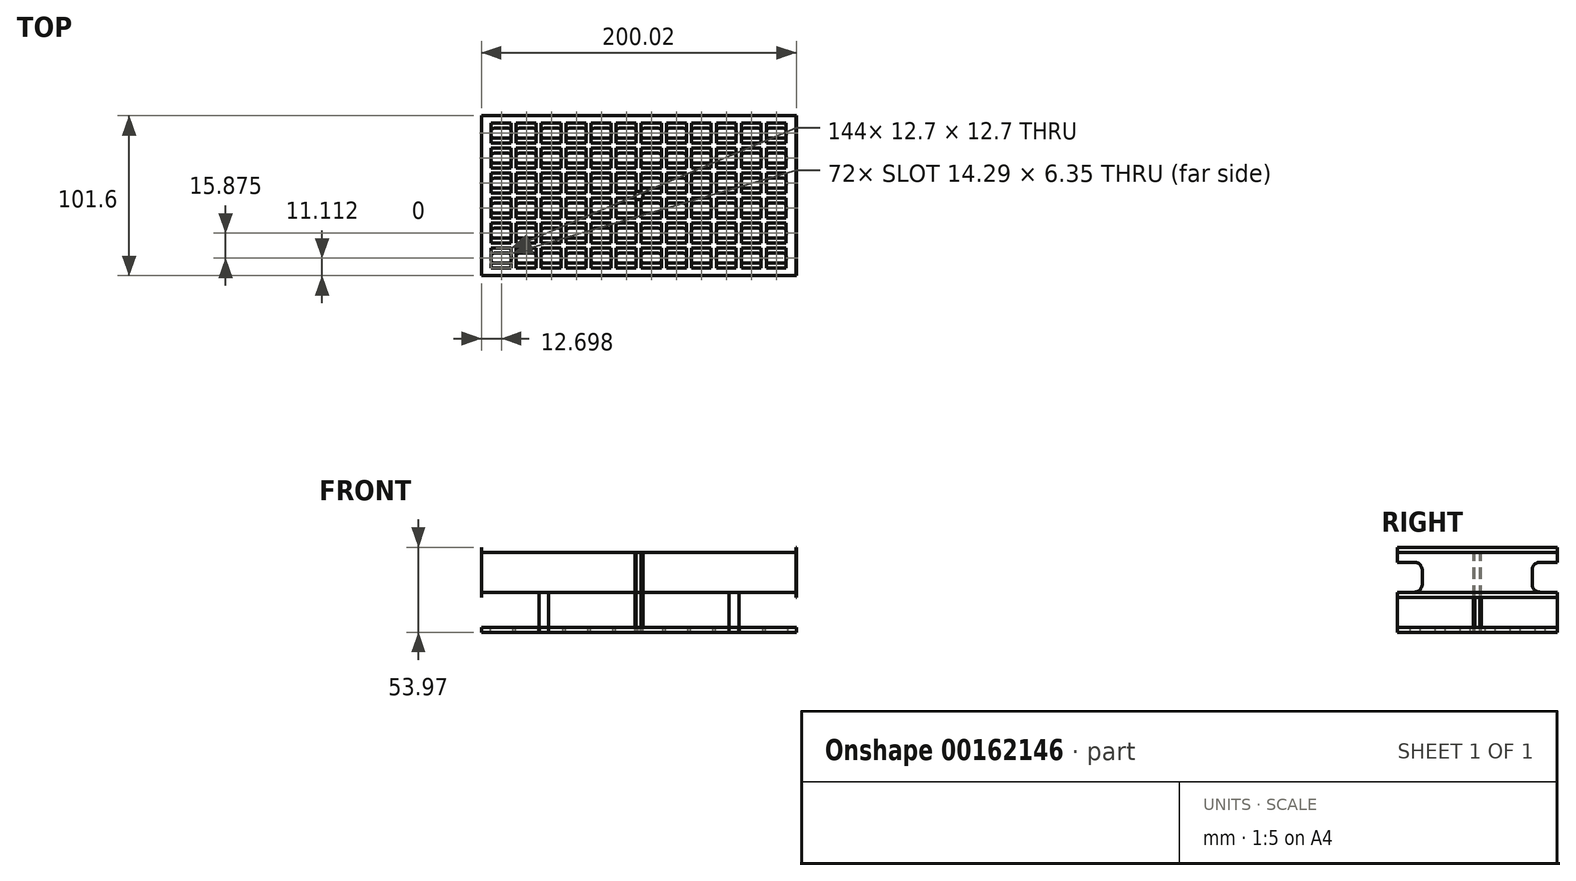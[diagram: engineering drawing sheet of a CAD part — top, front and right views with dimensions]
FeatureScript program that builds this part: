
annotation { "Feature Type Name" : "Feature", "Feature Type Description" : "" }
export const myFeature = defineFeature(function(context is Context, id is Id, definition is map)
    precondition{}
    {
        {
            var Q0;
            Q0=qCreatedBy(makeId("Top.planeOp"),FACE);
            var sketch = newSketch(context, id + "F0", { "sketchPlane" : qUnion([Q0])});
            skLineSegment(sketch, "E0.bottom", {"start": v(100.01, -50.8) * mm, "end": v(-100.01, -50.8) * mm});
            skLineSegment(sketch, "E0.top", {"start": v(100.01, 50.8) * mm, "end": v(-100.01, 50.8) * mm});
            skLineSegment(sketch, "E0.left", {"start": v(100.01, -50.8) * mm, "end": v(100.01, 50.8) * mm});
            skLineSegment(sketch, "E0.right", {"start": v(-100.01, -50.8) * mm, "end": v(-100.01, 50.8) * mm});
            skLineSegment(sketch, "E1", {"start": v(0, 0) * mm, "end": v(-14.29, 0) * mm});
            skLineSegment(sketch, "E2", {"start": v(-14.29, 0) * mm, "end": v(-14.29, -1.59) * mm});
            skLineSegment(sketch, "E3.bottom", {"start": v(-14.29, -1.59) * mm, "end": v(-1.59, -1.59) * mm});
            skLineSegment(sketch, "E3.top", {"start": v(-14.29, -14.29) * mm, "end": v(-1.59, -14.29) * mm});
            skLineSegment(sketch, "E3.left", {"start": v(-14.29, -1.59) * mm, "end": v(-14.29, -14.29) * mm});
            skLineSegment(sketch, "E3.right", {"start": v(-1.59, -1.59) * mm, "end": v(-1.59, -14.29) * mm});
            skLineSegment(sketch, "E4.0.1.0", {"start": v(-14.29, -17.46) * mm, "end": v(-1.59, -17.46) * mm});
            skLineSegment(sketch, "E4.0.1.1", {"start": v(-14.29, -17.46) * mm, "end": v(-14.29, -30.16) * mm});
            skLineSegment(sketch, "E4.0.1.2", {"start": v(-1.59, -17.46) * mm, "end": v(-1.59, -30.16) * mm});
            skLineSegment(sketch, "E4.0.1.3", {"start": v(-14.29, -30.16) * mm, "end": v(-1.59, -30.16) * mm});
            skLineSegment(sketch, "E4.0.2.0", {"start": v(-14.29, -33.34) * mm, "end": v(-1.59, -33.34) * mm});
            skLineSegment(sketch, "E4.0.2.1", {"start": v(-14.29, -33.34) * mm, "end": v(-14.29, -46.04) * mm});
            skLineSegment(sketch, "E4.0.2.2", {"start": v(-1.59, -33.34) * mm, "end": v(-1.59, -46.04) * mm});
            skLineSegment(sketch, "E4.0.2.3", {"start": v(-14.29, -46.04) * mm, "end": v(-1.59, -46.04) * mm});
            skLineSegment(sketch, "E4.1.0.0", {"start": v(-30.16, -1.59) * mm, "end": v(-17.46, -1.59) * mm});
            skLineSegment(sketch, "E4.1.0.1", {"start": v(-30.16, -1.59) * mm, "end": v(-30.16, -14.29) * mm});
            skLineSegment(sketch, "E4.1.0.2", {"start": v(-17.46, -1.59) * mm, "end": v(-17.46, -14.29) * mm});
            skLineSegment(sketch, "E4.1.0.3", {"start": v(-30.16, -14.29) * mm, "end": v(-17.46, -14.29) * mm});
            skLineSegment(sketch, "E4.1.1.0", {"start": v(-30.16, -17.46) * mm, "end": v(-17.46, -17.46) * mm});
            skLineSegment(sketch, "E4.1.1.1", {"start": v(-30.16, -17.46) * mm, "end": v(-30.16, -30.16) * mm});
            skLineSegment(sketch, "E4.1.1.2", {"start": v(-17.46, -17.46) * mm, "end": v(-17.46, -30.16) * mm});
            skLineSegment(sketch, "E4.1.1.3", {"start": v(-30.16, -30.16) * mm, "end": v(-17.46, -30.16) * mm});
            skLineSegment(sketch, "E4.1.2.0", {"start": v(-30.16, -33.34) * mm, "end": v(-17.46, -33.34) * mm});
            skLineSegment(sketch, "E4.1.2.1", {"start": v(-30.16, -33.34) * mm, "end": v(-30.16, -46.04) * mm});
            skLineSegment(sketch, "E4.1.2.2", {"start": v(-17.46, -33.34) * mm, "end": v(-17.46, -46.04) * mm});
            skLineSegment(sketch, "E4.1.2.3", {"start": v(-30.16, -46.04) * mm, "end": v(-17.46, -46.04) * mm});
            skLineSegment(sketch, "E4.2.0.0", {"start": v(-46.04, -1.59) * mm, "end": v(-33.34, -1.59) * mm});
            skLineSegment(sketch, "E4.2.0.1", {"start": v(-46.04, -1.59) * mm, "end": v(-46.04, -14.29) * mm});
            skLineSegment(sketch, "E4.2.0.2", {"start": v(-33.34, -1.59) * mm, "end": v(-33.34, -14.29) * mm});
            skLineSegment(sketch, "E4.2.0.3", {"start": v(-46.04, -14.29) * mm, "end": v(-33.34, -14.29) * mm});
            skLineSegment(sketch, "E4.2.1.0", {"start": v(-46.04, -17.46) * mm, "end": v(-33.34, -17.46) * mm});
            skLineSegment(sketch, "E4.2.1.1", {"start": v(-46.04, -17.46) * mm, "end": v(-46.04, -30.16) * mm});
            skLineSegment(sketch, "E4.2.1.2", {"start": v(-33.34, -17.46) * mm, "end": v(-33.34, -30.16) * mm});
            skLineSegment(sketch, "E4.2.1.3", {"start": v(-46.04, -30.16) * mm, "end": v(-33.34, -30.16) * mm});
            skLineSegment(sketch, "E4.2.2.0", {"start": v(-46.04, -33.34) * mm, "end": v(-33.34, -33.34) * mm});
            skLineSegment(sketch, "E4.2.2.1", {"start": v(-46.04, -33.34) * mm, "end": v(-46.04, -46.04) * mm});
            skLineSegment(sketch, "E4.2.2.2", {"start": v(-33.34, -33.34) * mm, "end": v(-33.34, -46.04) * mm});
            skLineSegment(sketch, "E4.2.2.3", {"start": v(-46.04, -46.04) * mm, "end": v(-33.34, -46.04) * mm});
            skLineSegment(sketch, "E4.3.0.0", {"start": v(-61.91, -1.59) * mm, "end": v(-49.21, -1.59) * mm});
            skLineSegment(sketch, "E4.3.0.1", {"start": v(-61.91, -1.59) * mm, "end": v(-61.91, -14.29) * mm});
            skLineSegment(sketch, "E4.3.0.2", {"start": v(-49.21, -1.59) * mm, "end": v(-49.21, -14.29) * mm});
            skLineSegment(sketch, "E4.3.0.3", {"start": v(-61.91, -14.29) * mm, "end": v(-49.21, -14.29) * mm});
            skLineSegment(sketch, "E4.3.1.0", {"start": v(-61.91, -17.46) * mm, "end": v(-49.21, -17.46) * mm});
            skLineSegment(sketch, "E4.3.1.1", {"start": v(-61.91, -17.46) * mm, "end": v(-61.91, -30.16) * mm});
            skLineSegment(sketch, "E4.3.1.2", {"start": v(-49.21, -17.46) * mm, "end": v(-49.21, -30.16) * mm});
            skLineSegment(sketch, "E4.3.1.3", {"start": v(-61.91, -30.16) * mm, "end": v(-49.21, -30.16) * mm});
            skLineSegment(sketch, "E4.3.2.0", {"start": v(-61.91, -33.34) * mm, "end": v(-49.21, -33.34) * mm});
            skLineSegment(sketch, "E4.3.2.1", {"start": v(-61.91, -33.34) * mm, "end": v(-61.91, -46.04) * mm});
            skLineSegment(sketch, "E4.3.2.2", {"start": v(-49.21, -33.34) * mm, "end": v(-49.21, -46.04) * mm});
            skLineSegment(sketch, "E4.3.2.3", {"start": v(-61.91, -46.04) * mm, "end": v(-49.21, -46.04) * mm});
            skLineSegment(sketch, "E4.4.0.0", {"start": v(-77.79, -1.59) * mm, "end": v(-65.09, -1.59) * mm});
            skLineSegment(sketch, "E4.4.0.1", {"start": v(-77.79, -1.59) * mm, "end": v(-77.79, -14.29) * mm});
            skLineSegment(sketch, "E4.4.0.2", {"start": v(-65.09, -1.59) * mm, "end": v(-65.09, -14.29) * mm});
            skLineSegment(sketch, "E4.4.0.3", {"start": v(-77.79, -14.29) * mm, "end": v(-65.09, -14.29) * mm});
            skLineSegment(sketch, "E4.4.1.0", {"start": v(-77.79, -17.46) * mm, "end": v(-65.09, -17.46) * mm});
            skLineSegment(sketch, "E4.4.1.1", {"start": v(-77.79, -17.46) * mm, "end": v(-77.79, -30.16) * mm});
            skLineSegment(sketch, "E4.4.1.2", {"start": v(-65.09, -17.46) * mm, "end": v(-65.09, -30.16) * mm});
            skLineSegment(sketch, "E4.4.1.3", {"start": v(-77.79, -30.16) * mm, "end": v(-65.09, -30.16) * mm});
            skLineSegment(sketch, "E4.4.2.0", {"start": v(-77.79, -33.34) * mm, "end": v(-65.09, -33.34) * mm});
            skLineSegment(sketch, "E4.4.2.1", {"start": v(-77.79, -33.34) * mm, "end": v(-77.79, -46.04) * mm});
            skLineSegment(sketch, "E4.4.2.2", {"start": v(-65.09, -33.34) * mm, "end": v(-65.09, -46.04) * mm});
            skLineSegment(sketch, "E4.4.2.3", {"start": v(-77.79, -46.04) * mm, "end": v(-65.09, -46.04) * mm});
            skLineSegment(sketch, "E4.5.0.0", {"start": v(-93.66, -1.59) * mm, "end": v(-80.96, -1.59) * mm});
            skLineSegment(sketch, "E4.5.0.1", {"start": v(-93.66, -1.59) * mm, "end": v(-93.66, -14.29) * mm});
            skLineSegment(sketch, "E4.5.0.2", {"start": v(-80.96, -1.59) * mm, "end": v(-80.96, -14.29) * mm});
            skLineSegment(sketch, "E4.5.0.3", {"start": v(-93.66, -14.29) * mm, "end": v(-80.96, -14.29) * mm});
            skLineSegment(sketch, "E4.5.1.0", {"start": v(-93.66, -17.46) * mm, "end": v(-80.96, -17.46) * mm});
            skLineSegment(sketch, "E4.5.1.1", {"start": v(-93.66, -17.46) * mm, "end": v(-93.66, -30.16) * mm});
            skLineSegment(sketch, "E4.5.1.2", {"start": v(-80.96, -17.46) * mm, "end": v(-80.96, -30.16) * mm});
            skLineSegment(sketch, "E4.5.1.3", {"start": v(-93.66, -30.16) * mm, "end": v(-80.96, -30.16) * mm});
            skLineSegment(sketch, "E4.5.2.0", {"start": v(-93.66, -33.34) * mm, "end": v(-80.96, -33.34) * mm});
            skLineSegment(sketch, "E4.5.2.1", {"start": v(-93.66, -33.34) * mm, "end": v(-93.66, -46.04) * mm});
            skLineSegment(sketch, "E4.5.2.2", {"start": v(-80.96, -33.34) * mm, "end": v(-80.96, -46.04) * mm});
            skLineSegment(sketch, "E4.5.2.3", {"start": v(-93.66, -46.04) * mm, "end": v(-80.96, -46.04) * mm});
            skLineSegment(sketch, "E4.direction1", {"start": v(-14.29, -1.59) * mm, "end": v(-30.16, -1.59) * mm, "construction": true});
            skLineSegment(sketch, "E4.direction2", {"start": v(-14.29, -1.59) * mm, "end": v(-14.29, -17.46) * mm, "construction": true});
            skLineSegment(sketch, "E5.MirrorCS", {"start": v(-14.29, 0) * mm, "end": v(-14.29, 1.59) * mm});
            skLineSegment(sketch, "E6.MirrorCS", {"start": v(-30.16, 1.59) * mm, "end": v(-17.46, 1.59) * mm});
            skLineSegment(sketch, "E7.MirrorCS", {"start": v(-14.29, 1.59) * mm, "end": v(-14.29, 14.29) * mm});
            skLineSegment(sketch, "E8.MirrorCS", {"start": v(-93.66, 1.59) * mm, "end": v(-80.96, 1.59) * mm});
            skLineSegment(sketch, "E9.MirrorCS", {"start": v(-46.04, 17.46) * mm, "end": v(-46.04, 30.16) * mm});
            skLineSegment(sketch, "E10.MirrorCS", {"start": v(-93.66, 30.16) * mm, "end": v(-80.96, 30.16) * mm});
            skLineSegment(sketch, "E11.MirrorCS", {"start": v(-30.16, 30.16) * mm, "end": v(-17.46, 30.16) * mm});
            skLineSegment(sketch, "E12.MirrorCS", {"start": v(-46.04, 14.29) * mm, "end": v(-33.34, 14.29) * mm});
            skLineSegment(sketch, "E13.MirrorCS", {"start": v(-61.91, 33.34) * mm, "end": v(-61.91, 46.04) * mm});
            skLineSegment(sketch, "E14.MirrorCS", {"start": v(-61.91, 30.16) * mm, "end": v(-49.21, 30.16) * mm});
            skLineSegment(sketch, "E15.MirrorCS", {"start": v(-93.66, 1.59) * mm, "end": v(-93.66, 14.29) * mm});
            skLineSegment(sketch, "E16.MirrorCS", {"start": v(-30.16, 33.34) * mm, "end": v(-17.46, 33.34) * mm});
            skLineSegment(sketch, "E17.MirrorCS", {"start": v(-80.96, 17.46) * mm, "end": v(-80.96, 30.16) * mm});
            skLineSegment(sketch, "E18.MirrorCS", {"start": v(-17.46, 17.46) * mm, "end": v(-17.46, 30.16) * mm});
            skLineSegment(sketch, "E19.MirrorCS", {"start": v(-61.91, 33.34) * mm, "end": v(-49.21, 33.34) * mm});
            skLineSegment(sketch, "E20.MirrorCS", {"start": v(-46.04, 17.46) * mm, "end": v(-33.34, 17.46) * mm});
            skLineSegment(sketch, "E21.MirrorCS", {"start": v(-1.59, 33.34) * mm, "end": v(-1.59, 46.04) * mm});
            skLineSegment(sketch, "E22.MirrorCS", {"start": v(-46.04, 33.34) * mm, "end": v(-46.04, 46.04) * mm});
            skLineSegment(sketch, "E23.MirrorCS", {"start": v(-1.59, 17.46) * mm, "end": v(-1.59, 30.16) * mm});
            skLineSegment(sketch, "E24.MirrorCS", {"start": v(-14.29, 17.46) * mm, "end": v(-1.59, 17.46) * mm});
            skLineSegment(sketch, "E25.MirrorCS", {"start": v(-14.29, 14.29) * mm, "end": v(-1.59, 14.29) * mm});
            skLineSegment(sketch, "E26.MirrorCS", {"start": v(-14.29, 1.59) * mm, "end": v(-1.59, 1.59) * mm});
            skLineSegment(sketch, "E27.MirrorCS", {"start": v(-14.29, 30.16) * mm, "end": v(-1.59, 30.16) * mm});
            skLineSegment(sketch, "E28.MirrorCS", {"start": v(-46.04, 33.34) * mm, "end": v(-33.34, 33.34) * mm});
            skLineSegment(sketch, "E29.MirrorCS", {"start": v(-77.79, 1.59) * mm, "end": v(-65.09, 1.59) * mm});
            skLineSegment(sketch, "E30.MirrorCS", {"start": v(-33.34, 17.46) * mm, "end": v(-33.34, 30.16) * mm});
            skLineSegment(sketch, "E31.MirrorCS", {"start": v(-49.21, 33.34) * mm, "end": v(-49.21, 46.04) * mm});
            skLineSegment(sketch, "E32.MirrorCS", {"start": v(-93.66, 46.04) * mm, "end": v(-80.96, 46.04) * mm});
            skLineSegment(sketch, "E33.MirrorCS", {"start": v(-30.16, 1.59) * mm, "end": v(-30.16, 14.29) * mm});
            skLineSegment(sketch, "E34.MirrorCS", {"start": v(-93.66, 33.34) * mm, "end": v(-80.96, 33.34) * mm});
            skLineSegment(sketch, "E35.MirrorCS", {"start": v(-61.91, 1.59) * mm, "end": v(-49.21, 1.59) * mm});
            skLineSegment(sketch, "E36.MirrorCS", {"start": v(-77.79, 17.46) * mm, "end": v(-65.09, 17.46) * mm});
            skLineSegment(sketch, "E37.MirrorCS", {"start": v(-46.04, 46.04) * mm, "end": v(-33.34, 46.04) * mm});
            skLineSegment(sketch, "E38.MirrorCS", {"start": v(-77.79, 14.29) * mm, "end": v(-65.09, 14.29) * mm});
            skLineSegment(sketch, "E39.MirrorCS", {"start": v(-1.59, 1.59) * mm, "end": v(-1.59, 14.29) * mm});
            skLineSegment(sketch, "E40.MirrorCS", {"start": v(-77.79, 17.46) * mm, "end": v(-77.79, 30.16) * mm});
            skLineSegment(sketch, "E41.MirrorCS", {"start": v(-61.91, 1.59) * mm, "end": v(-61.91, 14.29) * mm});
            skLineSegment(sketch, "E42.MirrorCS", {"start": v(-30.16, 33.34) * mm, "end": v(-30.16, 46.04) * mm});
            skLineSegment(sketch, "E43.MirrorCS", {"start": v(-14.29, 17.46) * mm, "end": v(-14.29, 30.16) * mm});
            skLineSegment(sketch, "E44.MirrorCS", {"start": v(-93.66, 33.34) * mm, "end": v(-93.66, 46.04) * mm});
            skLineSegment(sketch, "E45.MirrorCS", {"start": v(-17.46, 1.59) * mm, "end": v(-17.46, 14.29) * mm});
            skLineSegment(sketch, "E46.MirrorCS", {"start": v(-80.96, 1.59) * mm, "end": v(-80.96, 14.29) * mm});
            skLineSegment(sketch, "E47.MirrorCS", {"start": v(-77.79, 30.16) * mm, "end": v(-65.09, 30.16) * mm});
            skLineSegment(sketch, "E48.MirrorCS", {"start": v(-61.91, 14.29) * mm, "end": v(-49.21, 14.29) * mm});
            skLineSegment(sketch, "E49.MirrorCS", {"start": v(-65.09, 33.34) * mm, "end": v(-65.09, 46.04) * mm});
            skLineSegment(sketch, "E50.MirrorCS", {"start": v(-49.21, 17.46) * mm, "end": v(-49.21, 30.16) * mm});
            skLineSegment(sketch, "E51.MirrorCS", {"start": v(-33.34, 1.59) * mm, "end": v(-33.34, 14.29) * mm});
            skLineSegment(sketch, "E52.MirrorCS", {"start": v(-30.16, 17.46) * mm, "end": v(-17.46, 17.46) * mm});
            skLineSegment(sketch, "E53.MirrorCS", {"start": v(-14.29, 1.59) * mm, "end": v(-14.29, 17.46) * mm, "construction": true});
            skLineSegment(sketch, "E54.MirrorCS", {"start": v(-77.79, 33.34) * mm, "end": v(-77.79, 46.04) * mm});
            skLineSegment(sketch, "E55.MirrorCS", {"start": v(-93.66, 17.46) * mm, "end": v(-80.96, 17.46) * mm});
            skLineSegment(sketch, "E56.MirrorCS", {"start": v(-30.16, 46.04) * mm, "end": v(-17.46, 46.04) * mm});
            skLineSegment(sketch, "E57.MirrorCS", {"start": v(-61.91, 17.46) * mm, "end": v(-61.91, 30.16) * mm});
            skLineSegment(sketch, "E58.MirrorCS", {"start": v(-46.04, 1.59) * mm, "end": v(-46.04, 14.29) * mm});
            skLineSegment(sketch, "E59.MirrorCS", {"start": v(-14.29, 33.34) * mm, "end": v(-1.59, 33.34) * mm});
            skLineSegment(sketch, "E60.MirrorCS", {"start": v(-14.29, 33.34) * mm, "end": v(-14.29, 46.04) * mm});
            skLineSegment(sketch, "E61.MirrorCS", {"start": v(-77.79, 1.59) * mm, "end": v(-77.79, 14.29) * mm});
            skLineSegment(sketch, "E62.MirrorCS", {"start": v(-30.16, 17.46) * mm, "end": v(-30.16, 30.16) * mm});
            skLineSegment(sketch, "E63.MirrorCS", {"start": v(-65.09, 17.46) * mm, "end": v(-65.09, 30.16) * mm});
            skLineSegment(sketch, "E64.MirrorCS", {"start": v(-49.21, 1.59) * mm, "end": v(-49.21, 14.29) * mm});
            skLineSegment(sketch, "E65.MirrorCS", {"start": v(-17.46, 33.34) * mm, "end": v(-17.46, 46.04) * mm});
            skLineSegment(sketch, "E66.MirrorCS", {"start": v(-93.66, 17.46) * mm, "end": v(-93.66, 30.16) * mm});
            skLineSegment(sketch, "E67.MirrorCS", {"start": v(-80.96, 33.34) * mm, "end": v(-80.96, 46.04) * mm});
            skLineSegment(sketch, "E68.MirrorCS", {"start": v(-30.16, 14.29) * mm, "end": v(-17.46, 14.29) * mm});
            skLineSegment(sketch, "E69.MirrorCS", {"start": v(-77.79, 33.34) * mm, "end": v(-65.09, 33.34) * mm});
            skLineSegment(sketch, "E70.MirrorCS", {"start": v(-14.29, 1.59) * mm, "end": v(-30.16, 1.59) * mm, "construction": true});
            skLineSegment(sketch, "E71.MirrorCS", {"start": v(-93.66, 14.29) * mm, "end": v(-80.96, 14.29) * mm});
            skLineSegment(sketch, "E72.MirrorCS", {"start": v(-61.91, 46.04) * mm, "end": v(-49.21, 46.04) * mm});
            skLineSegment(sketch, "E73.MirrorCS", {"start": v(-61.91, 17.46) * mm, "end": v(-49.21, 17.46) * mm});
            skLineSegment(sketch, "E74.MirrorCS", {"start": v(-65.09, 1.59) * mm, "end": v(-65.09, 14.29) * mm});
            skLineSegment(sketch, "E75.MirrorCS", {"start": v(-46.04, 30.16) * mm, "end": v(-33.34, 30.16) * mm});
            skLineSegment(sketch, "E76.MirrorCS", {"start": v(-46.04, 1.59) * mm, "end": v(-33.34, 1.59) * mm});
            skLineSegment(sketch, "E77.MirrorCS", {"start": v(-33.34, 33.34) * mm, "end": v(-33.34, 46.04) * mm});
            skLineSegment(sketch, "E78.MirrorCS", {"start": v(-77.79, 46.04) * mm, "end": v(-65.09, 46.04) * mm});
            skLineSegment(sketch, "E79.MirrorCS", {"start": v(-14.29, 46.04) * mm, "end": v(-1.59, 46.04) * mm});
            skLineSegment(sketch, "E80.MirrorCS", {"start": v(14.29, 0) * mm, "end": v(14.29, 1.59) * mm});
            skLineSegment(sketch, "E81.MirrorCS", {"start": v(14.29, 0) * mm, "end": v(14.29, -1.59) * mm});
            skLineSegment(sketch, "E82.MirrorCS", {"start": v(30.16, 1.59) * mm, "end": v(17.46, 1.59) * mm});
            skLineSegment(sketch, "E83.MirrorCS", {"start": v(0, 0) * mm, "end": v(14.29, 0) * mm});
            skLineSegment(sketch, "E84.MirrorCS", {"start": v(14.29, -1.59) * mm, "end": v(14.29, -14.29) * mm});
            skLineSegment(sketch, "E85.MirrorCS", {"start": v(30.16, -1.59) * mm, "end": v(17.46, -1.59) * mm});
            skLineSegment(sketch, "E86.MirrorCS", {"start": v(14.29, 1.59) * mm, "end": v(30.16, 1.59) * mm, "construction": true});
            skLineSegment(sketch, "E87.MirrorCS", {"start": v(14.29, 1.59) * mm, "end": v(14.29, 14.29) * mm});
            skLineSegment(sketch, "E88.MirrorCS", {"start": v(1.59, 33.34) * mm, "end": v(1.59, 46.04) * mm});
            skLineSegment(sketch, "E89.MirrorCS", {"start": v(77.79, 17.46) * mm, "end": v(65.09, 17.46) * mm});
            skLineSegment(sketch, "E90.MirrorCS", {"start": v(30.16, 17.46) * mm, "end": v(17.46, 17.46) * mm});
            skLineSegment(sketch, "E91.MirrorCS", {"start": v(30.16, 14.29) * mm, "end": v(17.46, 14.29) * mm});
            skLineSegment(sketch, "E92.MirrorCS", {"start": v(46.04, -17.46) * mm, "end": v(33.34, -17.46) * mm});
            skLineSegment(sketch, "E93.MirrorCS", {"start": v(61.91, -33.34) * mm, "end": v(49.21, -33.34) * mm});
            skLineSegment(sketch, "E94.MirrorCS", {"start": v(65.09, -1.59) * mm, "end": v(65.09, -14.29) * mm});
            skLineSegment(sketch, "E95.MirrorCS", {"start": v(14.29, 17.46) * mm, "end": v(14.29, 30.16) * mm});
            skLineSegment(sketch, "E96.MirrorCS", {"start": v(14.29, 30.16) * mm, "end": v(1.59, 30.16) * mm});
            skLineSegment(sketch, "E97.MirrorCS", {"start": v(33.34, -33.34) * mm, "end": v(33.34, -46.04) * mm});
            skLineSegment(sketch, "E98.MirrorCS", {"start": v(17.46, -17.46) * mm, "end": v(17.46, -30.16) * mm});
            skLineSegment(sketch, "E99.MirrorCS", {"start": v(30.16, 33.34) * mm, "end": v(30.16, 46.04) * mm});
            skLineSegment(sketch, "E100.MirrorCS", {"start": v(65.09, 1.59) * mm, "end": v(65.09, 14.29) * mm});
            skLineSegment(sketch, "E101.MirrorCS", {"start": v(61.91, -1.59) * mm, "end": v(61.91, -14.29) * mm});
            skLineSegment(sketch, "E102.MirrorCS", {"start": v(17.46, 1.59) * mm, "end": v(17.46, 14.29) * mm});
            skLineSegment(sketch, "E103.MirrorCS", {"start": v(93.66, -30.16) * mm, "end": v(80.96, -30.16) * mm});
            skLineSegment(sketch, "E104.MirrorCS", {"start": v(30.16, -1.59) * mm, "end": v(30.16, -14.29) * mm});
            skLineSegment(sketch, "E105.MirrorCS", {"start": v(46.04, 30.16) * mm, "end": v(33.34, 30.16) * mm});
            skLineSegment(sketch, "E106.MirrorCS", {"start": v(14.29, 33.34) * mm, "end": v(1.59, 33.34) * mm});
            skLineSegment(sketch, "E107.MirrorCS", {"start": v(46.04, 46.04) * mm, "end": v(33.34, 46.04) * mm});
            skLineSegment(sketch, "E108.MirrorCS", {"start": v(33.34, 33.34) * mm, "end": v(33.34, 46.04) * mm});
            skLineSegment(sketch, "E109.MirrorCS", {"start": v(77.79, 1.59) * mm, "end": v(77.79, 14.29) * mm});
            skLineSegment(sketch, "E110.MirrorCS", {"start": v(93.66, -46.04) * mm, "end": v(80.96, -46.04) * mm});
            skLineSegment(sketch, "E111.MirrorCS", {"start": v(77.79, -30.16) * mm, "end": v(65.09, -30.16) * mm});
            skLineSegment(sketch, "E112.MirrorCS", {"start": v(61.91, -14.29) * mm, "end": v(49.21, -14.29) * mm});
            skLineSegment(sketch, "E113.MirrorCS", {"start": v(49.21, -33.34) * mm, "end": v(49.21, -46.04) * mm});
            skLineSegment(sketch, "E114.MirrorCS", {"start": v(30.16, -46.04) * mm, "end": v(17.46, -46.04) * mm});
            skLineSegment(sketch, "E115.MirrorCS", {"start": v(65.09, 17.46) * mm, "end": v(65.09, 30.16) * mm});
            skLineSegment(sketch, "E116.MirrorCS", {"start": v(77.79, 30.16) * mm, "end": v(65.09, 30.16) * mm});
            skLineSegment(sketch, "E117.MirrorCS", {"start": v(49.21, 33.34) * mm, "end": v(49.21, 46.04) * mm});
            skLineSegment(sketch, "E118.MirrorCS", {"start": v(30.16, 33.34) * mm, "end": v(17.46, 33.34) * mm});
            skLineSegment(sketch, "E119.MirrorCS", {"start": v(30.16, -14.29) * mm, "end": v(17.46, -14.29) * mm});
            skLineSegment(sketch, "E120.MirrorCS", {"start": v(93.66, 1.59) * mm, "end": v(80.96, 1.59) * mm});
            skLineSegment(sketch, "E121.MirrorCS", {"start": v(46.04, -30.16) * mm, "end": v(33.34, -30.16) * mm});
            skLineSegment(sketch, "E122.MirrorCS", {"start": v(14.29, 46.04) * mm, "end": v(1.59, 46.04) * mm});
            skLineSegment(sketch, "E123.MirrorCS", {"start": v(65.09, -17.46) * mm, "end": v(65.09, -30.16) * mm});
            skLineSegment(sketch, "E124.MirrorCS", {"start": v(49.21, -1.59) * mm, "end": v(49.21, -14.29) * mm});
            skLineSegment(sketch, "E125.MirrorCS", {"start": v(17.46, -33.34) * mm, "end": v(17.46, -46.04) * mm});
            skLineSegment(sketch, "E126.MirrorCS", {"start": v(80.96, 1.59) * mm, "end": v(80.96, 14.29) * mm});
            skLineSegment(sketch, "E127.MirrorCS", {"start": v(33.34, 17.46) * mm, "end": v(33.34, 30.16) * mm});
            skLineSegment(sketch, "E128.MirrorCS", {"start": v(93.66, 1.59) * mm, "end": v(93.66, 14.29) * mm});
            skLineSegment(sketch, "E129.MirrorCS", {"start": v(80.96, -33.34) * mm, "end": v(80.96, -46.04) * mm});
            skLineSegment(sketch, "E130.MirrorCS", {"start": v(77.79, 46.04) * mm, "end": v(65.09, 46.04) * mm});
            skLineSegment(sketch, "E131.MirrorCS", {"start": v(30.16, 17.46) * mm, "end": v(30.16, 30.16) * mm});
            skLineSegment(sketch, "E132.MirrorCS", {"start": v(93.66, 17.46) * mm, "end": v(80.96, 17.46) * mm});
            skLineSegment(sketch, "E133.MirrorCS", {"start": v(14.29, -1.59) * mm, "end": v(30.16, -1.59) * mm, "construction": true});
            skLineSegment(sketch, "E134.MirrorCS", {"start": v(77.79, -33.34) * mm, "end": v(65.09, -33.34) * mm});
            skLineSegment(sketch, "E135.MirrorCS", {"start": v(61.91, -17.46) * mm, "end": v(49.21, -17.46) * mm});
            skLineSegment(sketch, "E136.MirrorCS", {"start": v(46.04, -1.59) * mm, "end": v(33.34, -1.59) * mm});
            skLineSegment(sketch, "E137.MirrorCS", {"start": v(77.79, -17.46) * mm, "end": v(65.09, -17.46) * mm});
            skLineSegment(sketch, "E138.MirrorCS", {"start": v(61.91, -1.59) * mm, "end": v(49.21, -1.59) * mm});
            skLineSegment(sketch, "E139.MirrorCS", {"start": v(49.21, 1.59) * mm, "end": v(49.21, 14.29) * mm});
            skLineSegment(sketch, "E140.MirrorCS", {"start": v(61.91, 14.29) * mm, "end": v(49.21, 14.29) * mm});
            skLineSegment(sketch, "E141.MirrorCS", {"start": v(93.66, 46.04) * mm, "end": v(80.96, 46.04) * mm});
            skLineSegment(sketch, "E142.MirrorCS", {"start": v(80.96, 17.46) * mm, "end": v(80.96, 30.16) * mm});
            skLineSegment(sketch, "E143.MirrorCS", {"start": v(46.04, -33.34) * mm, "end": v(46.04, -46.04) * mm});
            skLineSegment(sketch, "E144.MirrorCS", {"start": v(61.91, 1.59) * mm, "end": v(61.91, 14.29) * mm});
            skLineSegment(sketch, "E145.MirrorCS", {"start": v(93.66, 30.16) * mm, "end": v(80.96, 30.16) * mm});
            skLineSegment(sketch, "E146.MirrorCS", {"start": v(61.91, 17.46) * mm, "end": v(49.21, 17.46) * mm});
            skLineSegment(sketch, "E147.MirrorCS", {"start": v(61.91, 17.46) * mm, "end": v(61.91, 30.16) * mm});
            skLineSegment(sketch, "E148.MirrorCS", {"start": v(30.16, 30.16) * mm, "end": v(17.46, 30.16) * mm});
            skLineSegment(sketch, "E149.MirrorCS", {"start": v(80.96, -17.46) * mm, "end": v(80.96, -30.16) * mm});
            skLineSegment(sketch, "E150.MirrorCS", {"start": v(46.04, 1.59) * mm, "end": v(46.04, 14.29) * mm});
            skLineSegment(sketch, "E151.MirrorCS", {"start": v(14.29, -1.59) * mm, "end": v(14.29, -17.46) * mm, "construction": true});
            skLineSegment(sketch, "E152.MirrorCS", {"start": v(77.79, -33.34) * mm, "end": v(77.79, -46.04) * mm});
            skLineSegment(sketch, "E153.MirrorCS", {"start": v(61.91, -17.46) * mm, "end": v(61.91, -30.16) * mm});
            skLineSegment(sketch, "E154.MirrorCS", {"start": v(46.04, -1.59) * mm, "end": v(46.04, -14.29) * mm});
            skLineSegment(sketch, "E155.MirrorCS", {"start": v(77.79, -17.46) * mm, "end": v(77.79, -30.16) * mm});
            skLineSegment(sketch, "E156.MirrorCS", {"start": v(30.16, -33.34) * mm, "end": v(30.16, -46.04) * mm});
            skLineSegment(sketch, "E157.MirrorCS", {"start": v(77.79, 1.59) * mm, "end": v(65.09, 1.59) * mm});
            skLineSegment(sketch, "E158.MirrorCS", {"start": v(61.91, 30.16) * mm, "end": v(49.21, 30.16) * mm});
            skLineSegment(sketch, "E159.MirrorCS", {"start": v(93.66, -33.34) * mm, "end": v(93.66, -46.04) * mm});
            skLineSegment(sketch, "E160.MirrorCS", {"start": v(17.46, 33.34) * mm, "end": v(17.46, 46.04) * mm});
            skLineSegment(sketch, "E161.MirrorCS", {"start": v(65.09, 33.34) * mm, "end": v(65.09, 46.04) * mm});
            skLineSegment(sketch, "E162.MirrorCS", {"start": v(30.16, 1.59) * mm, "end": v(30.16, 14.29) * mm});
            skLineSegment(sketch, "E163.MirrorCS", {"start": v(93.66, -1.59) * mm, "end": v(80.96, -1.59) * mm});
            skLineSegment(sketch, "E164.MirrorCS", {"start": v(77.79, 33.34) * mm, "end": v(77.79, 46.04) * mm});
            skLineSegment(sketch, "E165.MirrorCS", {"start": v(61.91, 33.34) * mm, "end": v(49.21, 33.34) * mm});
            skLineSegment(sketch, "E166.MirrorCS", {"start": v(77.79, 14.29) * mm, "end": v(65.09, 14.29) * mm});
            skLineSegment(sketch, "E167.MirrorCS", {"start": v(33.34, -17.46) * mm, "end": v(33.34, -30.16) * mm});
            skLineSegment(sketch, "E168.MirrorCS", {"start": v(14.29, -14.29) * mm, "end": v(1.59, -14.29) * mm});
            skLineSegment(sketch, "E169.MirrorCS", {"start": v(80.96, -1.59) * mm, "end": v(80.96, -14.29) * mm});
            skLineSegment(sketch, "E170.MirrorCS", {"start": v(93.66, 33.34) * mm, "end": v(80.96, 33.34) * mm});
            skLineSegment(sketch, "E171.MirrorCS", {"start": v(93.66, 17.46) * mm, "end": v(93.66, 30.16) * mm});
            skLineSegment(sketch, "E172.MirrorCS", {"start": v(49.21, 17.46) * mm, "end": v(49.21, 30.16) * mm});
            skLineSegment(sketch, "E173.MirrorCS", {"start": v(17.46, -1.59) * mm, "end": v(17.46, -14.29) * mm});
            skLineSegment(sketch, "E174.MirrorCS", {"start": v(1.59, -17.46) * mm, "end": v(1.59, -30.16) * mm});
            skLineSegment(sketch, "E175.MirrorCS", {"start": v(14.29, 33.34) * mm, "end": v(14.29, 46.04) * mm});
            skLineSegment(sketch, "E176.MirrorCS", {"start": v(14.29, -1.59) * mm, "end": v(1.59, -1.59) * mm});
            skLineSegment(sketch, "E177.MirrorCS", {"start": v(46.04, 1.59) * mm, "end": v(33.34, 1.59) * mm});
            skLineSegment(sketch, "E178.MirrorCS", {"start": v(93.66, -33.34) * mm, "end": v(80.96, -33.34) * mm});
            skLineSegment(sketch, "E179.MirrorCS", {"start": v(61.91, 33.34) * mm, "end": v(61.91, 46.04) * mm});
            skLineSegment(sketch, "E180.MirrorCS", {"start": v(33.34, -1.59) * mm, "end": v(33.34, -14.29) * mm});
            skLineSegment(sketch, "E181.MirrorCS", {"start": v(93.66, -17.46) * mm, "end": v(93.66, -30.16) * mm});
            skLineSegment(sketch, "E182.MirrorCS", {"start": v(14.29, 1.59) * mm, "end": v(1.59, 1.59) * mm});
            skLineSegment(sketch, "E183.MirrorCS", {"start": v(30.16, -17.46) * mm, "end": v(30.16, -30.16) * mm});
            skLineSegment(sketch, "E184.MirrorCS", {"start": v(14.29, -17.46) * mm, "end": v(14.29, -30.16) * mm});
            skLineSegment(sketch, "E185.MirrorCS", {"start": v(49.21, -17.46) * mm, "end": v(49.21, -30.16) * mm});
            skLineSegment(sketch, "E186.MirrorCS", {"start": v(30.16, -30.16) * mm, "end": v(17.46, -30.16) * mm});
            skLineSegment(sketch, "E187.MirrorCS", {"start": v(65.09, -33.34) * mm, "end": v(65.09, -46.04) * mm});
            skLineSegment(sketch, "E188.MirrorCS", {"start": v(46.04, 33.34) * mm, "end": v(46.04, 46.04) * mm});
            skLineSegment(sketch, "E189.MirrorCS", {"start": v(46.04, 33.34) * mm, "end": v(33.34, 33.34) * mm});
            skLineSegment(sketch, "E190.MirrorCS", {"start": v(93.66, 33.34) * mm, "end": v(93.66, 46.04) * mm});
            skLineSegment(sketch, "E191.MirrorCS", {"start": v(30.16, -33.34) * mm, "end": v(17.46, -33.34) * mm});
            skLineSegment(sketch, "E192.MirrorCS", {"start": v(14.29, 1.59) * mm, "end": v(14.29, 17.46) * mm, "construction": true});
            skLineSegment(sketch, "E193.MirrorCS", {"start": v(14.29, -17.46) * mm, "end": v(1.59, -17.46) * mm});
            skLineSegment(sketch, "E194.MirrorCS", {"start": v(77.79, -1.59) * mm, "end": v(77.79, -14.29) * mm});
            skLineSegment(sketch, "E195.MirrorCS", {"start": v(77.79, 33.34) * mm, "end": v(65.09, 33.34) * mm});
            skLineSegment(sketch, "E196.MirrorCS", {"start": v(14.29, 17.46) * mm, "end": v(1.59, 17.46) * mm});
            skLineSegment(sketch, "E197.MirrorCS", {"start": v(46.04, -17.46) * mm, "end": v(46.04, -30.16) * mm});
            skLineSegment(sketch, "E198.MirrorCS", {"start": v(1.59, -33.34) * mm, "end": v(1.59, -46.04) * mm});
            skLineSegment(sketch, "E199.MirrorCS", {"start": v(1.59, 1.59) * mm, "end": v(1.59, 14.29) * mm});
            skLineSegment(sketch, "E200.MirrorCS", {"start": v(61.91, -46.04) * mm, "end": v(49.21, -46.04) * mm});
            skLineSegment(sketch, "E201.MirrorCS", {"start": v(93.66, 14.29) * mm, "end": v(80.96, 14.29) * mm});
            skLineSegment(sketch, "E202.MirrorCS", {"start": v(77.79, -14.29) * mm, "end": v(65.09, -14.29) * mm});
            skLineSegment(sketch, "E203.MirrorCS", {"start": v(1.59, -1.59) * mm, "end": v(1.59, -14.29) * mm});
            skLineSegment(sketch, "E204.MirrorCS", {"start": v(61.91, 1.59) * mm, "end": v(49.21, 1.59) * mm});
            skLineSegment(sketch, "E205.MirrorCS", {"start": v(46.04, 17.46) * mm, "end": v(33.34, 17.46) * mm});
            skLineSegment(sketch, "E206.MirrorCS", {"start": v(33.34, 1.59) * mm, "end": v(33.34, 14.29) * mm});
            skLineSegment(sketch, "E207.MirrorCS", {"start": v(46.04, -14.29) * mm, "end": v(33.34, -14.29) * mm});
            skLineSegment(sketch, "E208.MirrorCS", {"start": v(80.96, 33.34) * mm, "end": v(80.96, 46.04) * mm});
            skLineSegment(sketch, "E209.MirrorCS", {"start": v(61.91, -30.16) * mm, "end": v(49.21, -30.16) * mm});
            skLineSegment(sketch, "E210.MirrorCS", {"start": v(77.79, -46.04) * mm, "end": v(65.09, -46.04) * mm});
            skLineSegment(sketch, "E211.MirrorCS", {"start": v(14.29, -46.04) * mm, "end": v(1.59, -46.04) * mm});
            skLineSegment(sketch, "E212.MirrorCS", {"start": v(14.29, 14.29) * mm, "end": v(1.59, 14.29) * mm});
            skLineSegment(sketch, "E213.MirrorCS", {"start": v(77.79, 17.46) * mm, "end": v(77.79, 30.16) * mm});
            skLineSegment(sketch, "E214.MirrorCS", {"start": v(30.16, 46.04) * mm, "end": v(17.46, 46.04) * mm});
            skLineSegment(sketch, "E215.MirrorCS", {"start": v(93.66, -17.46) * mm, "end": v(80.96, -17.46) * mm});
            skLineSegment(sketch, "E216.MirrorCS", {"start": v(46.04, -33.34) * mm, "end": v(33.34, -33.34) * mm});
            skLineSegment(sketch, "E217.MirrorCS", {"start": v(77.79, -1.59) * mm, "end": v(65.09, -1.59) * mm});
            skLineSegment(sketch, "E218.MirrorCS", {"start": v(61.91, 46.04) * mm, "end": v(49.21, 46.04) * mm});
            skLineSegment(sketch, "E219.MirrorCS", {"start": v(61.91, -33.34) * mm, "end": v(61.91, -46.04) * mm});
            skLineSegment(sketch, "E220.MirrorCS", {"start": v(1.59, 17.46) * mm, "end": v(1.59, 30.16) * mm});
            skLineSegment(sketch, "E221.MirrorCS", {"start": v(30.16, -17.46) * mm, "end": v(17.46, -17.46) * mm});
            skLineSegment(sketch, "E222.MirrorCS", {"start": v(93.66, -14.29) * mm, "end": v(80.96, -14.29) * mm});
            skLineSegment(sketch, "E223.MirrorCS", {"start": v(93.66, -1.59) * mm, "end": v(93.66, -14.29) * mm});
            skLineSegment(sketch, "E224.MirrorCS", {"start": v(46.04, 17.46) * mm, "end": v(46.04, 30.16) * mm});
            skLineSegment(sketch, "E225.MirrorCS", {"start": v(46.04, -46.04) * mm, "end": v(33.34, -46.04) * mm});
            skLineSegment(sketch, "E226.MirrorCS", {"start": v(46.04, 14.29) * mm, "end": v(33.34, 14.29) * mm});
            skLineSegment(sketch, "E227.MirrorCS", {"start": v(14.29, -33.34) * mm, "end": v(14.29, -46.04) * mm});
            skLineSegment(sketch, "E228.MirrorCS", {"start": v(14.29, -33.34) * mm, "end": v(1.59, -33.34) * mm});
            skLineSegment(sketch, "E229.MirrorCS", {"start": v(14.29, -30.16) * mm, "end": v(1.59, -30.16) * mm});
            skLineSegment(sketch, "E230.MirrorCS", {"start": v(17.46, 17.46) * mm, "end": v(17.46, 30.16) * mm});
            skSolve(sketch);
        }
        {
            var Q0;
            Q0=makeQuery(id+"F0.imprint","IMPRINT",FACE,{"disambiguationData":[TD([[makeQuery(id+"F0.imprint","IMPRINT",EDGE,{"derivedFrom":sQuery(id+"F0.wireOp",EDGE,"E0.bottom")}),-1.0]])]});
            extrude(context, id + "F1", {"entities" : qUnion([Q0]), "oppositeDirection" : true, "depth" : 1 / 203.2 * mm});
        }
        {
            var Q0;
            Q0=qCreatedBy(makeId("Top.planeOp"),FACE);
            cPlane(context, id + "F2", {"entities" : qUnion([Q0]), "cplaneType" : CPlaneType.OFFSET, "offset" : 25.4 * mm, "width" : 152.4 * mm, "height" : 152.4 * mm});
        }
        {
            var Q0;
            Q0=qCreatedBy(id+"F2.planeOp",FACE);
            var sketch = newSketch(context, id + "F3", { "sketchPlane" : qUnion([Q0])});
            skLineSegment(sketch, "E231.bottom", {"start": v(100.01, -50.8) * mm, "end": v(-100.01, -50.8) * mm});
            skLineSegment(sketch, "E231.top", {"start": v(100.01, 50.8) * mm, "end": v(-100.01, 50.8) * mm});
            skLineSegment(sketch, "E231.left", {"start": v(100.01, -50.8) * mm, "end": v(100.01, 50.8) * mm});
            skLineSegment(sketch, "E231.right", {"start": v(-100.01, -50.8) * mm, "end": v(-100.01, 50.8) * mm});
            skLineSegment(sketch, "E232", {"start": v(0, 0) * mm, "end": v(-14.29, 0) * mm});
            skLineSegment(sketch, "E233", {"start": v(-14.29, 0) * mm, "end": v(-14.29, -1.59) * mm});
            skLineSegment(sketch, "E234.bottom", {"start": v(-14.29, -1.59) * mm, "end": v(-1.59, -1.59) * mm});
            skLineSegment(sketch, "E234.top", {"start": v(-14.29, -14.29) * mm, "end": v(-1.59, -14.29) * mm});
            skLineSegment(sketch, "E234.left", {"start": v(-14.29, -1.59) * mm, "end": v(-14.29, -14.29) * mm});
            skLineSegment(sketch, "E234.right", {"start": v(-1.59, -1.59) * mm, "end": v(-1.59, -14.29) * mm});
            skLineSegment(sketch, "E235.0.1.0", {"start": v(-14.29, -17.46) * mm, "end": v(-1.59, -17.46) * mm});
            skLineSegment(sketch, "E235.0.1.1", {"start": v(-14.29, -17.46) * mm, "end": v(-14.29, -30.16) * mm});
            skLineSegment(sketch, "E235.0.1.2", {"start": v(-1.59, -17.46) * mm, "end": v(-1.59, -30.16) * mm});
            skLineSegment(sketch, "E235.0.1.3", {"start": v(-14.29, -30.16) * mm, "end": v(-1.59, -30.16) * mm});
            skLineSegment(sketch, "E235.0.2.0", {"start": v(-14.29, -33.34) * mm, "end": v(-1.59, -33.34) * mm});
            skLineSegment(sketch, "E235.0.2.1", {"start": v(-14.29, -33.34) * mm, "end": v(-14.29, -46.04) * mm});
            skLineSegment(sketch, "E235.0.2.2", {"start": v(-1.59, -33.34) * mm, "end": v(-1.59, -46.04) * mm});
            skLineSegment(sketch, "E235.0.2.3", {"start": v(-14.29, -46.04) * mm, "end": v(-1.59, -46.04) * mm});
            skLineSegment(sketch, "E235.1.0.0", {"start": v(-30.16, -1.59) * mm, "end": v(-17.46, -1.59) * mm});
            skLineSegment(sketch, "E235.1.0.1", {"start": v(-30.16, -1.59) * mm, "end": v(-30.16, -14.29) * mm});
            skLineSegment(sketch, "E235.1.0.2", {"start": v(-17.46, -1.59) * mm, "end": v(-17.46, -14.29) * mm});
            skLineSegment(sketch, "E235.1.0.3", {"start": v(-30.16, -14.29) * mm, "end": v(-17.46, -14.29) * mm});
            skLineSegment(sketch, "E235.1.1.0", {"start": v(-30.16, -17.46) * mm, "end": v(-17.46, -17.46) * mm});
            skLineSegment(sketch, "E235.1.1.1", {"start": v(-30.16, -17.46) * mm, "end": v(-30.16, -30.16) * mm});
            skLineSegment(sketch, "E235.1.1.2", {"start": v(-17.46, -17.46) * mm, "end": v(-17.46, -30.16) * mm});
            skLineSegment(sketch, "E235.1.1.3", {"start": v(-30.16, -30.16) * mm, "end": v(-17.46, -30.16) * mm});
            skLineSegment(sketch, "E235.1.2.0", {"start": v(-30.16, -33.34) * mm, "end": v(-17.46, -33.34) * mm});
            skLineSegment(sketch, "E235.1.2.1", {"start": v(-30.16, -33.34) * mm, "end": v(-30.16, -46.04) * mm});
            skLineSegment(sketch, "E235.1.2.2", {"start": v(-17.46, -33.34) * mm, "end": v(-17.46, -46.04) * mm});
            skLineSegment(sketch, "E235.1.2.3", {"start": v(-30.16, -46.04) * mm, "end": v(-17.46, -46.04) * mm});
            skLineSegment(sketch, "E235.2.0.0", {"start": v(-46.04, -1.59) * mm, "end": v(-33.34, -1.59) * mm});
            skLineSegment(sketch, "E235.2.0.1", {"start": v(-46.04, -1.59) * mm, "end": v(-46.04, -14.29) * mm});
            skLineSegment(sketch, "E235.2.0.2", {"start": v(-33.34, -1.59) * mm, "end": v(-33.34, -14.29) * mm});
            skLineSegment(sketch, "E235.2.0.3", {"start": v(-46.04, -14.29) * mm, "end": v(-33.34, -14.29) * mm});
            skLineSegment(sketch, "E235.2.1.0", {"start": v(-46.04, -17.46) * mm, "end": v(-33.34, -17.46) * mm});
            skLineSegment(sketch, "E235.2.1.1", {"start": v(-46.04, -17.46) * mm, "end": v(-46.04, -30.16) * mm});
            skLineSegment(sketch, "E235.2.1.2", {"start": v(-33.34, -17.46) * mm, "end": v(-33.34, -30.16) * mm});
            skLineSegment(sketch, "E235.2.1.3", {"start": v(-46.04, -30.16) * mm, "end": v(-33.34, -30.16) * mm});
            skLineSegment(sketch, "E235.2.2.0", {"start": v(-46.04, -33.34) * mm, "end": v(-33.34, -33.34) * mm});
            skLineSegment(sketch, "E235.2.2.1", {"start": v(-46.04, -33.34) * mm, "end": v(-46.04, -46.04) * mm});
            skLineSegment(sketch, "E235.2.2.2", {"start": v(-33.34, -33.34) * mm, "end": v(-33.34, -46.04) * mm});
            skLineSegment(sketch, "E235.2.2.3", {"start": v(-46.04, -46.04) * mm, "end": v(-33.34, -46.04) * mm});
            skLineSegment(sketch, "E235.3.0.0", {"start": v(-61.91, -1.59) * mm, "end": v(-49.21, -1.59) * mm});
            skLineSegment(sketch, "E235.3.0.1", {"start": v(-61.91, -1.59) * mm, "end": v(-61.91, -14.29) * mm});
            skLineSegment(sketch, "E235.3.0.2", {"start": v(-49.21, -1.59) * mm, "end": v(-49.21, -14.29) * mm});
            skLineSegment(sketch, "E235.3.0.3", {"start": v(-61.91, -14.29) * mm, "end": v(-49.21, -14.29) * mm});
            skLineSegment(sketch, "E235.3.1.0", {"start": v(-61.91, -17.46) * mm, "end": v(-49.21, -17.46) * mm});
            skLineSegment(sketch, "E235.3.1.1", {"start": v(-61.91, -17.46) * mm, "end": v(-61.91, -30.16) * mm});
            skLineSegment(sketch, "E235.3.1.2", {"start": v(-49.21, -17.46) * mm, "end": v(-49.21, -30.16) * mm});
            skLineSegment(sketch, "E235.3.1.3", {"start": v(-61.91, -30.16) * mm, "end": v(-49.21, -30.16) * mm});
            skLineSegment(sketch, "E235.3.2.0", {"start": v(-61.91, -33.34) * mm, "end": v(-49.21, -33.34) * mm});
            skLineSegment(sketch, "E235.3.2.1", {"start": v(-61.91, -33.34) * mm, "end": v(-61.91, -46.04) * mm});
            skLineSegment(sketch, "E235.3.2.2", {"start": v(-49.21, -33.34) * mm, "end": v(-49.21, -46.04) * mm});
            skLineSegment(sketch, "E235.3.2.3", {"start": v(-61.91, -46.04) * mm, "end": v(-49.21, -46.04) * mm});
            skLineSegment(sketch, "E235.4.0.0", {"start": v(-77.79, -1.59) * mm, "end": v(-65.09, -1.59) * mm});
            skLineSegment(sketch, "E235.4.0.1", {"start": v(-77.79, -1.59) * mm, "end": v(-77.79, -14.29) * mm});
            skLineSegment(sketch, "E235.4.0.2", {"start": v(-65.09, -1.59) * mm, "end": v(-65.09, -14.29) * mm});
            skLineSegment(sketch, "E235.4.0.3", {"start": v(-77.79, -14.29) * mm, "end": v(-65.09, -14.29) * mm});
            skLineSegment(sketch, "E235.4.1.0", {"start": v(-77.79, -17.46) * mm, "end": v(-65.09, -17.46) * mm});
            skLineSegment(sketch, "E235.4.1.1", {"start": v(-77.79, -17.46) * mm, "end": v(-77.79, -30.16) * mm});
            skLineSegment(sketch, "E235.4.1.2", {"start": v(-65.09, -17.46) * mm, "end": v(-65.09, -30.16) * mm});
            skLineSegment(sketch, "E235.4.1.3", {"start": v(-77.79, -30.16) * mm, "end": v(-65.09, -30.16) * mm});
            skLineSegment(sketch, "E235.4.2.0", {"start": v(-77.79, -33.34) * mm, "end": v(-65.09, -33.34) * mm});
            skLineSegment(sketch, "E235.4.2.1", {"start": v(-77.79, -33.34) * mm, "end": v(-77.79, -46.04) * mm});
            skLineSegment(sketch, "E235.4.2.2", {"start": v(-65.09, -33.34) * mm, "end": v(-65.09, -46.04) * mm});
            skLineSegment(sketch, "E235.4.2.3", {"start": v(-77.79, -46.04) * mm, "end": v(-65.09, -46.04) * mm});
            skLineSegment(sketch, "E235.5.0.0", {"start": v(-93.66, -1.59) * mm, "end": v(-80.96, -1.59) * mm});
            skLineSegment(sketch, "E235.5.0.1", {"start": v(-93.66, -1.59) * mm, "end": v(-93.66, -14.29) * mm});
            skLineSegment(sketch, "E235.5.0.2", {"start": v(-80.96, -1.59) * mm, "end": v(-80.96, -14.29) * mm});
            skLineSegment(sketch, "E235.5.0.3", {"start": v(-93.66, -14.29) * mm, "end": v(-80.96, -14.29) * mm});
            skLineSegment(sketch, "E235.5.1.0", {"start": v(-93.66, -17.46) * mm, "end": v(-80.96, -17.46) * mm});
            skLineSegment(sketch, "E235.5.1.1", {"start": v(-93.66, -17.46) * mm, "end": v(-93.66, -30.16) * mm});
            skLineSegment(sketch, "E235.5.1.2", {"start": v(-80.96, -17.46) * mm, "end": v(-80.96, -30.16) * mm});
            skLineSegment(sketch, "E235.5.1.3", {"start": v(-93.66, -30.16) * mm, "end": v(-80.96, -30.16) * mm});
            skLineSegment(sketch, "E235.5.2.0", {"start": v(-93.66, -33.34) * mm, "end": v(-80.96, -33.34) * mm});
            skLineSegment(sketch, "E235.5.2.1", {"start": v(-93.66, -33.34) * mm, "end": v(-93.66, -46.04) * mm});
            skLineSegment(sketch, "E235.5.2.2", {"start": v(-80.96, -33.34) * mm, "end": v(-80.96, -46.04) * mm});
            skLineSegment(sketch, "E235.5.2.3", {"start": v(-93.66, -46.04) * mm, "end": v(-80.96, -46.04) * mm});
            skLineSegment(sketch, "E235.direction1", {"start": v(-14.29, -1.59) * mm, "end": v(-30.16, -1.59) * mm, "construction": true});
            skLineSegment(sketch, "E235.direction2", {"start": v(-14.29, -1.59) * mm, "end": v(-14.29, -17.46) * mm, "construction": true});
            skLineSegment(sketch, "E236.MirrorCS", {"start": v(-14.29, 0) * mm, "end": v(-14.29, 1.59) * mm});
            skLineSegment(sketch, "E237.MirrorCS", {"start": v(-30.16, 1.59) * mm, "end": v(-17.46, 1.59) * mm});
            skLineSegment(sketch, "E238.MirrorCS", {"start": v(-14.29, 1.59) * mm, "end": v(-14.29, 14.29) * mm});
            skLineSegment(sketch, "E239.MirrorCS", {"start": v(-93.66, 1.59) * mm, "end": v(-80.96, 1.59) * mm});
            skLineSegment(sketch, "E240.MirrorCS", {"start": v(-46.04, 17.46) * mm, "end": v(-46.04, 30.16) * mm});
            skLineSegment(sketch, "E241.MirrorCS", {"start": v(-93.66, 30.16) * mm, "end": v(-80.96, 30.16) * mm});
            skLineSegment(sketch, "E242.MirrorCS", {"start": v(-30.16, 30.16) * mm, "end": v(-17.46, 30.16) * mm});
            skLineSegment(sketch, "E243.MirrorCS", {"start": v(-46.04, 14.29) * mm, "end": v(-33.34, 14.29) * mm});
            skLineSegment(sketch, "E244.MirrorCS", {"start": v(-61.91, 33.34) * mm, "end": v(-61.91, 46.04) * mm});
            skLineSegment(sketch, "E245.MirrorCS", {"start": v(-61.91, 30.16) * mm, "end": v(-49.21, 30.16) * mm});
            skLineSegment(sketch, "E246.MirrorCS", {"start": v(-93.66, 1.59) * mm, "end": v(-93.66, 14.29) * mm});
            skLineSegment(sketch, "E247.MirrorCS", {"start": v(-30.16, 33.34) * mm, "end": v(-17.46, 33.34) * mm});
            skLineSegment(sketch, "E248.MirrorCS", {"start": v(-80.96, 17.46) * mm, "end": v(-80.96, 30.16) * mm});
            skLineSegment(sketch, "E249.MirrorCS", {"start": v(-17.46, 17.46) * mm, "end": v(-17.46, 30.16) * mm});
            skLineSegment(sketch, "E250.MirrorCS", {"start": v(-61.91, 33.34) * mm, "end": v(-49.21, 33.34) * mm});
            skLineSegment(sketch, "E251.MirrorCS", {"start": v(-46.04, 17.46) * mm, "end": v(-33.34, 17.46) * mm});
            skLineSegment(sketch, "E252.MirrorCS", {"start": v(-1.59, 33.34) * mm, "end": v(-1.59, 46.04) * mm});
            skLineSegment(sketch, "E253.MirrorCS", {"start": v(-46.04, 33.34) * mm, "end": v(-46.04, 46.04) * mm});
            skLineSegment(sketch, "E254.MirrorCS", {"start": v(-1.59, 17.46) * mm, "end": v(-1.59, 30.16) * mm});
            skLineSegment(sketch, "E255.MirrorCS", {"start": v(-14.29, 17.46) * mm, "end": v(-1.59, 17.46) * mm});
            skLineSegment(sketch, "E256.MirrorCS", {"start": v(-14.29, 14.29) * mm, "end": v(-1.59, 14.29) * mm});
            skLineSegment(sketch, "E257.MirrorCS", {"start": v(-14.29, 1.59) * mm, "end": v(-1.59, 1.59) * mm});
            skLineSegment(sketch, "E258.MirrorCS", {"start": v(-14.29, 30.16) * mm, "end": v(-1.59, 30.16) * mm});
            skLineSegment(sketch, "E259.MirrorCS", {"start": v(-46.04, 33.34) * mm, "end": v(-33.34, 33.34) * mm});
            skLineSegment(sketch, "E260.MirrorCS", {"start": v(-77.79, 1.59) * mm, "end": v(-65.09, 1.59) * mm});
            skLineSegment(sketch, "E261.MirrorCS", {"start": v(-33.34, 17.46) * mm, "end": v(-33.34, 30.16) * mm});
            skLineSegment(sketch, "E262.MirrorCS", {"start": v(-49.21, 33.34) * mm, "end": v(-49.21, 46.04) * mm});
            skLineSegment(sketch, "E263.MirrorCS", {"start": v(-93.66, 46.04) * mm, "end": v(-80.96, 46.04) * mm});
            skLineSegment(sketch, "E264.MirrorCS", {"start": v(-30.16, 1.59) * mm, "end": v(-30.16, 14.29) * mm});
            skLineSegment(sketch, "E265.MirrorCS", {"start": v(-93.66, 33.34) * mm, "end": v(-80.96, 33.34) * mm});
            skLineSegment(sketch, "E266.MirrorCS", {"start": v(-61.91, 1.59) * mm, "end": v(-49.21, 1.59) * mm});
            skLineSegment(sketch, "E267.MirrorCS", {"start": v(-77.79, 17.46) * mm, "end": v(-65.09, 17.46) * mm});
            skLineSegment(sketch, "E268.MirrorCS", {"start": v(-46.04, 46.04) * mm, "end": v(-33.34, 46.04) * mm});
            skLineSegment(sketch, "E269.MirrorCS", {"start": v(-77.79, 14.29) * mm, "end": v(-65.09, 14.29) * mm});
            skLineSegment(sketch, "E270.MirrorCS", {"start": v(-1.59, 1.59) * mm, "end": v(-1.59, 14.29) * mm});
            skLineSegment(sketch, "E271.MirrorCS", {"start": v(-77.79, 17.46) * mm, "end": v(-77.79, 30.16) * mm});
            skLineSegment(sketch, "E272.MirrorCS", {"start": v(-61.91, 1.59) * mm, "end": v(-61.91, 14.29) * mm});
            skLineSegment(sketch, "E273.MirrorCS", {"start": v(-30.16, 33.34) * mm, "end": v(-30.16, 46.04) * mm});
            skLineSegment(sketch, "E274.MirrorCS", {"start": v(-14.29, 17.46) * mm, "end": v(-14.29, 30.16) * mm});
            skLineSegment(sketch, "E275.MirrorCS", {"start": v(-93.66, 33.34) * mm, "end": v(-93.66, 46.04) * mm});
            skLineSegment(sketch, "E276.MirrorCS", {"start": v(-17.46, 1.59) * mm, "end": v(-17.46, 14.29) * mm});
            skLineSegment(sketch, "E277.MirrorCS", {"start": v(-80.96, 1.59) * mm, "end": v(-80.96, 14.29) * mm});
            skLineSegment(sketch, "E278.MirrorCS", {"start": v(-77.79, 30.16) * mm, "end": v(-65.09, 30.16) * mm});
            skLineSegment(sketch, "E279.MirrorCS", {"start": v(-61.91, 14.29) * mm, "end": v(-49.21, 14.29) * mm});
            skLineSegment(sketch, "E280.MirrorCS", {"start": v(-65.09, 33.34) * mm, "end": v(-65.09, 46.04) * mm});
            skLineSegment(sketch, "E281.MirrorCS", {"start": v(-49.21, 17.46) * mm, "end": v(-49.21, 30.16) * mm});
            skLineSegment(sketch, "E282.MirrorCS", {"start": v(-33.34, 1.59) * mm, "end": v(-33.34, 14.29) * mm});
            skLineSegment(sketch, "E283.MirrorCS", {"start": v(-30.16, 17.46) * mm, "end": v(-17.46, 17.46) * mm});
            skLineSegment(sketch, "E284.MirrorCS", {"start": v(-14.29, 1.59) * mm, "end": v(-14.29, 17.46) * mm, "construction": true});
            skLineSegment(sketch, "E285.MirrorCS", {"start": v(-77.79, 33.34) * mm, "end": v(-77.79, 46.04) * mm});
            skLineSegment(sketch, "E286.MirrorCS", {"start": v(-93.66, 17.46) * mm, "end": v(-80.96, 17.46) * mm});
            skLineSegment(sketch, "E287.MirrorCS", {"start": v(-30.16, 46.04) * mm, "end": v(-17.46, 46.04) * mm});
            skLineSegment(sketch, "E288.MirrorCS", {"start": v(-61.91, 17.46) * mm, "end": v(-61.91, 30.16) * mm});
            skLineSegment(sketch, "E289.MirrorCS", {"start": v(-46.04, 1.59) * mm, "end": v(-46.04, 14.29) * mm});
            skLineSegment(sketch, "E290.MirrorCS", {"start": v(-14.29, 33.34) * mm, "end": v(-1.59, 33.34) * mm});
            skLineSegment(sketch, "E291.MirrorCS", {"start": v(-14.29, 33.34) * mm, "end": v(-14.29, 46.04) * mm});
            skLineSegment(sketch, "E292.MirrorCS", {"start": v(-77.79, 1.59) * mm, "end": v(-77.79, 14.29) * mm});
            skLineSegment(sketch, "E293.MirrorCS", {"start": v(-30.16, 17.46) * mm, "end": v(-30.16, 30.16) * mm});
            skLineSegment(sketch, "E294.MirrorCS", {"start": v(-65.09, 17.46) * mm, "end": v(-65.09, 30.16) * mm});
            skLineSegment(sketch, "E295.MirrorCS", {"start": v(-49.21, 1.59) * mm, "end": v(-49.21, 14.29) * mm});
            skLineSegment(sketch, "E296.MirrorCS", {"start": v(-17.46, 33.34) * mm, "end": v(-17.46, 46.04) * mm});
            skLineSegment(sketch, "E297.MirrorCS", {"start": v(-93.66, 17.46) * mm, "end": v(-93.66, 30.16) * mm});
            skLineSegment(sketch, "E298.MirrorCS", {"start": v(-80.96, 33.34) * mm, "end": v(-80.96, 46.04) * mm});
            skLineSegment(sketch, "E299.MirrorCS", {"start": v(-30.16, 14.29) * mm, "end": v(-17.46, 14.29) * mm});
            skLineSegment(sketch, "E300.MirrorCS", {"start": v(-77.79, 33.34) * mm, "end": v(-65.09, 33.34) * mm});
            skLineSegment(sketch, "E301.MirrorCS", {"start": v(-14.29, 1.59) * mm, "end": v(-30.16, 1.59) * mm, "construction": true});
            skLineSegment(sketch, "E302.MirrorCS", {"start": v(-93.66, 14.29) * mm, "end": v(-80.96, 14.29) * mm});
            skLineSegment(sketch, "E303.MirrorCS", {"start": v(-61.91, 46.04) * mm, "end": v(-49.21, 46.04) * mm});
            skLineSegment(sketch, "E304.MirrorCS", {"start": v(-61.91, 17.46) * mm, "end": v(-49.21, 17.46) * mm});
            skLineSegment(sketch, "E305.MirrorCS", {"start": v(-65.09, 1.59) * mm, "end": v(-65.09, 14.29) * mm});
            skLineSegment(sketch, "E306.MirrorCS", {"start": v(-46.04, 30.16) * mm, "end": v(-33.34, 30.16) * mm});
            skLineSegment(sketch, "E307.MirrorCS", {"start": v(-46.04, 1.59) * mm, "end": v(-33.34, 1.59) * mm});
            skLineSegment(sketch, "E308.MirrorCS", {"start": v(-33.34, 33.34) * mm, "end": v(-33.34, 46.04) * mm});
            skLineSegment(sketch, "E309.MirrorCS", {"start": v(-77.79, 46.04) * mm, "end": v(-65.09, 46.04) * mm});
            skLineSegment(sketch, "E310.MirrorCS", {"start": v(-14.29, 46.04) * mm, "end": v(-1.59, 46.04) * mm});
            skLineSegment(sketch, "E311.MirrorCS", {"start": v(14.29, 0) * mm, "end": v(14.29, 1.59) * mm});
            skLineSegment(sketch, "E312.MirrorCS", {"start": v(14.29, 0) * mm, "end": v(14.29, -1.59) * mm});
            skLineSegment(sketch, "E313.MirrorCS", {"start": v(30.16, 1.59) * mm, "end": v(17.46, 1.59) * mm});
            skLineSegment(sketch, "E314.MirrorCS", {"start": v(0, 0) * mm, "end": v(14.29, 0) * mm});
            skLineSegment(sketch, "E315.MirrorCS", {"start": v(14.29, -1.59) * mm, "end": v(14.29, -14.29) * mm});
            skLineSegment(sketch, "E316.MirrorCS", {"start": v(30.16, -1.59) * mm, "end": v(17.46, -1.59) * mm});
            skLineSegment(sketch, "E317.MirrorCS", {"start": v(14.29, 1.59) * mm, "end": v(30.16, 1.59) * mm, "construction": true});
            skLineSegment(sketch, "E318.MirrorCS", {"start": v(14.29, 1.59) * mm, "end": v(14.29, 14.29) * mm});
            skLineSegment(sketch, "E319.MirrorCS", {"start": v(1.59, 33.34) * mm, "end": v(1.59, 46.04) * mm});
            skLineSegment(sketch, "E320.MirrorCS", {"start": v(77.79, 17.46) * mm, "end": v(65.09, 17.46) * mm});
            skLineSegment(sketch, "E321.MirrorCS", {"start": v(30.16, 17.46) * mm, "end": v(17.46, 17.46) * mm});
            skLineSegment(sketch, "E322.MirrorCS", {"start": v(30.16, 14.29) * mm, "end": v(17.46, 14.29) * mm});
            skLineSegment(sketch, "E323.MirrorCS", {"start": v(46.04, -17.46) * mm, "end": v(33.34, -17.46) * mm});
            skLineSegment(sketch, "E324.MirrorCS", {"start": v(61.91, -33.34) * mm, "end": v(49.21, -33.34) * mm});
            skLineSegment(sketch, "E325.MirrorCS", {"start": v(65.09, -1.59) * mm, "end": v(65.09, -14.29) * mm});
            skLineSegment(sketch, "E326.MirrorCS", {"start": v(14.29, 17.46) * mm, "end": v(14.29, 30.16) * mm});
            skLineSegment(sketch, "E327.MirrorCS", {"start": v(14.29, 30.16) * mm, "end": v(1.59, 30.16) * mm});
            skLineSegment(sketch, "E328.MirrorCS", {"start": v(33.34, -33.34) * mm, "end": v(33.34, -46.04) * mm});
            skLineSegment(sketch, "E329.MirrorCS", {"start": v(17.46, -17.46) * mm, "end": v(17.46, -30.16) * mm});
            skLineSegment(sketch, "E330.MirrorCS", {"start": v(30.16, 33.34) * mm, "end": v(30.16, 46.04) * mm});
            skLineSegment(sketch, "E331.MirrorCS", {"start": v(65.09, 1.59) * mm, "end": v(65.09, 14.29) * mm});
            skLineSegment(sketch, "E332.MirrorCS", {"start": v(61.91, -1.59) * mm, "end": v(61.91, -14.29) * mm});
            skLineSegment(sketch, "E333.MirrorCS", {"start": v(17.46, 1.59) * mm, "end": v(17.46, 14.29) * mm});
            skLineSegment(sketch, "E334.MirrorCS", {"start": v(93.66, -30.16) * mm, "end": v(80.96, -30.16) * mm});
            skLineSegment(sketch, "E335.MirrorCS", {"start": v(30.16, -1.59) * mm, "end": v(30.16, -14.29) * mm});
            skLineSegment(sketch, "E336.MirrorCS", {"start": v(46.04, 30.16) * mm, "end": v(33.34, 30.16) * mm});
            skLineSegment(sketch, "E337.MirrorCS", {"start": v(14.29, 33.34) * mm, "end": v(1.59, 33.34) * mm});
            skLineSegment(sketch, "E338.MirrorCS", {"start": v(46.04, 46.04) * mm, "end": v(33.34, 46.04) * mm});
            skLineSegment(sketch, "E339.MirrorCS", {"start": v(33.34, 33.34) * mm, "end": v(33.34, 46.04) * mm});
            skLineSegment(sketch, "E340.MirrorCS", {"start": v(77.79, 1.59) * mm, "end": v(77.79, 14.29) * mm});
            skLineSegment(sketch, "E341.MirrorCS", {"start": v(93.66, -46.04) * mm, "end": v(80.96, -46.04) * mm});
            skLineSegment(sketch, "E342.MirrorCS", {"start": v(77.79, -30.16) * mm, "end": v(65.09, -30.16) * mm});
            skLineSegment(sketch, "E343.MirrorCS", {"start": v(61.91, -14.29) * mm, "end": v(49.21, -14.29) * mm});
            skLineSegment(sketch, "E344.MirrorCS", {"start": v(49.21, -33.34) * mm, "end": v(49.21, -46.04) * mm});
            skLineSegment(sketch, "E345.MirrorCS", {"start": v(30.16, -46.04) * mm, "end": v(17.46, -46.04) * mm});
            skLineSegment(sketch, "E346.MirrorCS", {"start": v(65.09, 17.46) * mm, "end": v(65.09, 30.16) * mm});
            skLineSegment(sketch, "E347.MirrorCS", {"start": v(77.79, 30.16) * mm, "end": v(65.09, 30.16) * mm});
            skLineSegment(sketch, "E348.MirrorCS", {"start": v(49.21, 33.34) * mm, "end": v(49.21, 46.04) * mm});
            skLineSegment(sketch, "E349.MirrorCS", {"start": v(30.16, 33.34) * mm, "end": v(17.46, 33.34) * mm});
            skLineSegment(sketch, "E350.MirrorCS", {"start": v(30.16, -14.29) * mm, "end": v(17.46, -14.29) * mm});
            skLineSegment(sketch, "E351.MirrorCS", {"start": v(93.66, 1.59) * mm, "end": v(80.96, 1.59) * mm});
            skLineSegment(sketch, "E352.MirrorCS", {"start": v(46.04, -30.16) * mm, "end": v(33.34, -30.16) * mm});
            skLineSegment(sketch, "E353.MirrorCS", {"start": v(14.29, 46.04) * mm, "end": v(1.59, 46.04) * mm});
            skLineSegment(sketch, "E354.MirrorCS", {"start": v(65.09, -17.46) * mm, "end": v(65.09, -30.16) * mm});
            skLineSegment(sketch, "E355.MirrorCS", {"start": v(49.21, -1.59) * mm, "end": v(49.21, -14.29) * mm});
            skLineSegment(sketch, "E356.MirrorCS", {"start": v(17.46, -33.34) * mm, "end": v(17.46, -46.04) * mm});
            skLineSegment(sketch, "E357.MirrorCS", {"start": v(80.96, 1.59) * mm, "end": v(80.96, 14.29) * mm});
            skLineSegment(sketch, "E358.MirrorCS", {"start": v(33.34, 17.46) * mm, "end": v(33.34, 30.16) * mm});
            skLineSegment(sketch, "E359.MirrorCS", {"start": v(93.66, 1.59) * mm, "end": v(93.66, 14.29) * mm});
            skLineSegment(sketch, "E360.MirrorCS", {"start": v(80.96, -33.34) * mm, "end": v(80.96, -46.04) * mm});
            skLineSegment(sketch, "E361.MirrorCS", {"start": v(77.79, 46.04) * mm, "end": v(65.09, 46.04) * mm});
            skLineSegment(sketch, "E362.MirrorCS", {"start": v(30.16, 17.46) * mm, "end": v(30.16, 30.16) * mm});
            skLineSegment(sketch, "E363.MirrorCS", {"start": v(93.66, 17.46) * mm, "end": v(80.96, 17.46) * mm});
            skLineSegment(sketch, "E364.MirrorCS", {"start": v(14.29, -1.59) * mm, "end": v(30.16, -1.59) * mm, "construction": true});
            skLineSegment(sketch, "E365.MirrorCS", {"start": v(77.79, -33.34) * mm, "end": v(65.09, -33.34) * mm});
            skLineSegment(sketch, "E366.MirrorCS", {"start": v(61.91, -17.46) * mm, "end": v(49.21, -17.46) * mm});
            skLineSegment(sketch, "E367.MirrorCS", {"start": v(46.04, -1.59) * mm, "end": v(33.34, -1.59) * mm});
            skLineSegment(sketch, "E368.MirrorCS", {"start": v(77.79, -17.46) * mm, "end": v(65.09, -17.46) * mm});
            skLineSegment(sketch, "E369.MirrorCS", {"start": v(61.91, -1.59) * mm, "end": v(49.21, -1.59) * mm});
            skLineSegment(sketch, "E370.MirrorCS", {"start": v(49.21, 1.59) * mm, "end": v(49.21, 14.29) * mm});
            skLineSegment(sketch, "E371.MirrorCS", {"start": v(61.91, 14.29) * mm, "end": v(49.21, 14.29) * mm});
            skLineSegment(sketch, "E372.MirrorCS", {"start": v(93.66, 46.04) * mm, "end": v(80.96, 46.04) * mm});
            skLineSegment(sketch, "E373.MirrorCS", {"start": v(80.96, 17.46) * mm, "end": v(80.96, 30.16) * mm});
            skLineSegment(sketch, "E374.MirrorCS", {"start": v(46.04, -33.34) * mm, "end": v(46.04, -46.04) * mm});
            skLineSegment(sketch, "E375.MirrorCS", {"start": v(61.91, 1.59) * mm, "end": v(61.91, 14.29) * mm});
            skLineSegment(sketch, "E376.MirrorCS", {"start": v(93.66, 30.16) * mm, "end": v(80.96, 30.16) * mm});
            skLineSegment(sketch, "E377.MirrorCS", {"start": v(61.91, 17.46) * mm, "end": v(49.21, 17.46) * mm});
            skLineSegment(sketch, "E378.MirrorCS", {"start": v(61.91, 17.46) * mm, "end": v(61.91, 30.16) * mm});
            skLineSegment(sketch, "E379.MirrorCS", {"start": v(30.16, 30.16) * mm, "end": v(17.46, 30.16) * mm});
            skLineSegment(sketch, "E380.MirrorCS", {"start": v(80.96, -17.46) * mm, "end": v(80.96, -30.16) * mm});
            skLineSegment(sketch, "E381.MirrorCS", {"start": v(46.04, 1.59) * mm, "end": v(46.04, 14.29) * mm});
            skLineSegment(sketch, "E382.MirrorCS", {"start": v(14.29, -1.59) * mm, "end": v(14.29, -17.46) * mm, "construction": true});
            skLineSegment(sketch, "E383.MirrorCS", {"start": v(77.79, -33.34) * mm, "end": v(77.79, -46.04) * mm});
            skLineSegment(sketch, "E384.MirrorCS", {"start": v(61.91, -17.46) * mm, "end": v(61.91, -30.16) * mm});
            skLineSegment(sketch, "E385.MirrorCS", {"start": v(46.04, -1.59) * mm, "end": v(46.04, -14.29) * mm});
            skLineSegment(sketch, "E386.MirrorCS", {"start": v(77.79, -17.46) * mm, "end": v(77.79, -30.16) * mm});
            skLineSegment(sketch, "E387.MirrorCS", {"start": v(30.16, -33.34) * mm, "end": v(30.16, -46.04) * mm});
            skLineSegment(sketch, "E388.MirrorCS", {"start": v(77.79, 1.59) * mm, "end": v(65.09, 1.59) * mm});
            skLineSegment(sketch, "E389.MirrorCS", {"start": v(61.91, 30.16) * mm, "end": v(49.21, 30.16) * mm});
            skLineSegment(sketch, "E390.MirrorCS", {"start": v(93.66, -33.34) * mm, "end": v(93.66, -46.04) * mm});
            skLineSegment(sketch, "E391.MirrorCS", {"start": v(17.46, 33.34) * mm, "end": v(17.46, 46.04) * mm});
            skLineSegment(sketch, "E392.MirrorCS", {"start": v(65.09, 33.34) * mm, "end": v(65.09, 46.04) * mm});
            skLineSegment(sketch, "E393.MirrorCS", {"start": v(30.16, 1.59) * mm, "end": v(30.16, 14.29) * mm});
            skLineSegment(sketch, "E394.MirrorCS", {"start": v(93.66, -1.59) * mm, "end": v(80.96, -1.59) * mm});
            skLineSegment(sketch, "E395.MirrorCS", {"start": v(77.79, 33.34) * mm, "end": v(77.79, 46.04) * mm});
            skLineSegment(sketch, "E396.MirrorCS", {"start": v(61.91, 33.34) * mm, "end": v(49.21, 33.34) * mm});
            skLineSegment(sketch, "E397.MirrorCS", {"start": v(77.79, 14.29) * mm, "end": v(65.09, 14.29) * mm});
            skLineSegment(sketch, "E398.MirrorCS", {"start": v(33.34, -17.46) * mm, "end": v(33.34, -30.16) * mm});
            skLineSegment(sketch, "E399.MirrorCS", {"start": v(14.29, -14.29) * mm, "end": v(1.59, -14.29) * mm});
            skLineSegment(sketch, "E400.MirrorCS", {"start": v(80.96, -1.59) * mm, "end": v(80.96, -14.29) * mm});
            skLineSegment(sketch, "E401.MirrorCS", {"start": v(93.66, 33.34) * mm, "end": v(80.96, 33.34) * mm});
            skLineSegment(sketch, "E402.MirrorCS", {"start": v(93.66, 17.46) * mm, "end": v(93.66, 30.16) * mm});
            skLineSegment(sketch, "E403.MirrorCS", {"start": v(49.21, 17.46) * mm, "end": v(49.21, 30.16) * mm});
            skLineSegment(sketch, "E404.MirrorCS", {"start": v(17.46, -1.59) * mm, "end": v(17.46, -14.29) * mm});
            skLineSegment(sketch, "E405.MirrorCS", {"start": v(1.59, -17.46) * mm, "end": v(1.59, -30.16) * mm});
            skLineSegment(sketch, "E406.MirrorCS", {"start": v(14.29, 33.34) * mm, "end": v(14.29, 46.04) * mm});
            skLineSegment(sketch, "E407.MirrorCS", {"start": v(14.29, -1.59) * mm, "end": v(1.59, -1.59) * mm});
            skLineSegment(sketch, "E408.MirrorCS", {"start": v(46.04, 1.59) * mm, "end": v(33.34, 1.59) * mm});
            skLineSegment(sketch, "E409.MirrorCS", {"start": v(93.66, -33.34) * mm, "end": v(80.96, -33.34) * mm});
            skLineSegment(sketch, "E410.MirrorCS", {"start": v(61.91, 33.34) * mm, "end": v(61.91, 46.04) * mm});
            skLineSegment(sketch, "E411.MirrorCS", {"start": v(33.34, -1.59) * mm, "end": v(33.34, -14.29) * mm});
            skLineSegment(sketch, "E412.MirrorCS", {"start": v(93.66, -17.46) * mm, "end": v(93.66, -30.16) * mm});
            skLineSegment(sketch, "E413.MirrorCS", {"start": v(14.29, 1.59) * mm, "end": v(1.59, 1.59) * mm});
            skLineSegment(sketch, "E414.MirrorCS", {"start": v(30.16, -17.46) * mm, "end": v(30.16, -30.16) * mm});
            skLineSegment(sketch, "E415.MirrorCS", {"start": v(14.29, -17.46) * mm, "end": v(14.29, -30.16) * mm});
            skLineSegment(sketch, "E416.MirrorCS", {"start": v(49.21, -17.46) * mm, "end": v(49.21, -30.16) * mm});
            skLineSegment(sketch, "E417.MirrorCS", {"start": v(30.16, -30.16) * mm, "end": v(17.46, -30.16) * mm});
            skLineSegment(sketch, "E418.MirrorCS", {"start": v(65.09, -33.34) * mm, "end": v(65.09, -46.04) * mm});
            skLineSegment(sketch, "E419.MirrorCS", {"start": v(46.04, 33.34) * mm, "end": v(46.04, 46.04) * mm});
            skLineSegment(sketch, "E420.MirrorCS", {"start": v(46.04, 33.34) * mm, "end": v(33.34, 33.34) * mm});
            skLineSegment(sketch, "E421.MirrorCS", {"start": v(93.66, 33.34) * mm, "end": v(93.66, 46.04) * mm});
            skLineSegment(sketch, "E422.MirrorCS", {"start": v(30.16, -33.34) * mm, "end": v(17.46, -33.34) * mm});
            skLineSegment(sketch, "E423.MirrorCS", {"start": v(14.29, 1.59) * mm, "end": v(14.29, 17.46) * mm, "construction": true});
            skLineSegment(sketch, "E424.MirrorCS", {"start": v(14.29, -17.46) * mm, "end": v(1.59, -17.46) * mm});
            skLineSegment(sketch, "E425.MirrorCS", {"start": v(77.79, -1.59) * mm, "end": v(77.79, -14.29) * mm});
            skLineSegment(sketch, "E426.MirrorCS", {"start": v(77.79, 33.34) * mm, "end": v(65.09, 33.34) * mm});
            skLineSegment(sketch, "E427.MirrorCS", {"start": v(14.29, 17.46) * mm, "end": v(1.59, 17.46) * mm});
            skLineSegment(sketch, "E428.MirrorCS", {"start": v(46.04, -17.46) * mm, "end": v(46.04, -30.16) * mm});
            skLineSegment(sketch, "E429.MirrorCS", {"start": v(1.59, -33.34) * mm, "end": v(1.59, -46.04) * mm});
            skLineSegment(sketch, "E430.MirrorCS", {"start": v(1.59, 1.59) * mm, "end": v(1.59, 14.29) * mm});
            skLineSegment(sketch, "E431.MirrorCS", {"start": v(61.91, -46.04) * mm, "end": v(49.21, -46.04) * mm});
            skLineSegment(sketch, "E432.MirrorCS", {"start": v(93.66, 14.29) * mm, "end": v(80.96, 14.29) * mm});
            skLineSegment(sketch, "E433.MirrorCS", {"start": v(77.79, -14.29) * mm, "end": v(65.09, -14.29) * mm});
            skLineSegment(sketch, "E434.MirrorCS", {"start": v(1.59, -1.59) * mm, "end": v(1.59, -14.29) * mm});
            skLineSegment(sketch, "E435.MirrorCS", {"start": v(61.91, 1.59) * mm, "end": v(49.21, 1.59) * mm});
            skLineSegment(sketch, "E436.MirrorCS", {"start": v(46.04, 17.46) * mm, "end": v(33.34, 17.46) * mm});
            skLineSegment(sketch, "E437.MirrorCS", {"start": v(33.34, 1.59) * mm, "end": v(33.34, 14.29) * mm});
            skLineSegment(sketch, "E438.MirrorCS", {"start": v(46.04, -14.29) * mm, "end": v(33.34, -14.29) * mm});
            skLineSegment(sketch, "E439.MirrorCS", {"start": v(80.96, 33.34) * mm, "end": v(80.96, 46.04) * mm});
            skLineSegment(sketch, "E440.MirrorCS", {"start": v(61.91, -30.16) * mm, "end": v(49.21, -30.16) * mm});
            skLineSegment(sketch, "E441.MirrorCS", {"start": v(77.79, -46.04) * mm, "end": v(65.09, -46.04) * mm});
            skLineSegment(sketch, "E442.MirrorCS", {"start": v(14.29, -46.04) * mm, "end": v(1.59, -46.04) * mm});
            skLineSegment(sketch, "E443.MirrorCS", {"start": v(14.29, 14.29) * mm, "end": v(1.59, 14.29) * mm});
            skLineSegment(sketch, "E444.MirrorCS", {"start": v(77.79, 17.46) * mm, "end": v(77.79, 30.16) * mm});
            skLineSegment(sketch, "E445.MirrorCS", {"start": v(30.16, 46.04) * mm, "end": v(17.46, 46.04) * mm});
            skLineSegment(sketch, "E446.MirrorCS", {"start": v(93.66, -17.46) * mm, "end": v(80.96, -17.46) * mm});
            skLineSegment(sketch, "E447.MirrorCS", {"start": v(46.04, -33.34) * mm, "end": v(33.34, -33.34) * mm});
            skLineSegment(sketch, "E448.MirrorCS", {"start": v(77.79, -1.59) * mm, "end": v(65.09, -1.59) * mm});
            skLineSegment(sketch, "E449.MirrorCS", {"start": v(61.91, 46.04) * mm, "end": v(49.21, 46.04) * mm});
            skLineSegment(sketch, "E450.MirrorCS", {"start": v(61.91, -33.34) * mm, "end": v(61.91, -46.04) * mm});
            skLineSegment(sketch, "E451.MirrorCS", {"start": v(1.59, 17.46) * mm, "end": v(1.59, 30.16) * mm});
            skLineSegment(sketch, "E452.MirrorCS", {"start": v(30.16, -17.46) * mm, "end": v(17.46, -17.46) * mm});
            skLineSegment(sketch, "E453.MirrorCS", {"start": v(93.66, -14.29) * mm, "end": v(80.96, -14.29) * mm});
            skLineSegment(sketch, "E454.MirrorCS", {"start": v(93.66, -1.59) * mm, "end": v(93.66, -14.29) * mm});
            skLineSegment(sketch, "E455.MirrorCS", {"start": v(46.04, 17.46) * mm, "end": v(46.04, 30.16) * mm});
            skLineSegment(sketch, "E456.MirrorCS", {"start": v(46.04, -46.04) * mm, "end": v(33.34, -46.04) * mm});
            skLineSegment(sketch, "E457.MirrorCS", {"start": v(46.04, 14.29) * mm, "end": v(33.34, 14.29) * mm});
            skLineSegment(sketch, "E458.MirrorCS", {"start": v(14.29, -33.34) * mm, "end": v(14.29, -46.04) * mm});
            skLineSegment(sketch, "E459.MirrorCS", {"start": v(14.29, -33.34) * mm, "end": v(1.59, -33.34) * mm});
            skLineSegment(sketch, "E460.MirrorCS", {"start": v(14.29, -30.16) * mm, "end": v(1.59, -30.16) * mm});
            skLineSegment(sketch, "E461.MirrorCS", {"start": v(17.46, 17.46) * mm, "end": v(17.46, 30.16) * mm});
            skSolve(sketch);
        }
        {
            var Q0;
            Q0 = qSketchRegion(id + "F3", true);
            var Q1;
            Q1 = qSketchRegion(id + "F3", true);
            extrude(context, id + "F4", {"entities" : qUnion([Q0, Q1]), "depth" : 1 / 203.2 * mm});
        }
        {
            var Q0;
            Q0=qCreatedBy(makeId("Top.planeOp"),FACE);
            cPlane(context, id + "F5", {"entities" : qUnion([Q0]), "cplaneType" : CPlaneType.OFFSET, "offset" : 25.4 * mm, "oppositeDirection" : true, "width" : 152.4 * mm, "height" : 152.4 * mm});
        }
        {
            var Q0;
            Q0=qCreatedBy(id+"F5.planeOp",FACE);
            var sketch = newSketch(context, id + "F6", { "sketchPlane" : qUnion([Q0])});
            skLineSegment(sketch, "E462.bottom", {"start": v(100.01, -50.8) * mm, "end": v(-100.01, -50.8) * mm});
            skLineSegment(sketch, "E462.top", {"start": v(100.01, 50.8) * mm, "end": v(-100.01, 50.8) * mm});
            skLineSegment(sketch, "E462.left", {"start": v(100.01, -50.8) * mm, "end": v(100.01, 50.8) * mm});
            skLineSegment(sketch, "E462.right", {"start": v(-100.01, -50.8) * mm, "end": v(-100.01, 50.8) * mm});
            skPoint(sketch, "E462.middle", {"position": v(0, 0) * mm});
            skLineSegment(sketch, "E463", {"start": v(0, 0) * mm, "end": v(-7.94, 0) * mm});
            skLineSegment(sketch, "E464", {"start": v(-7.94, 0) * mm, "end": v(-7.94, -7.94) * mm});
            skLineSegment(sketch, "E465.bottom", {"start": v(-3.97, -11.11) * mm, "end": v(-11.9, -11.11) * mm});
            skLineSegment(sketch, "E465.top", {"start": v(-3.97, -4.76) * mm, "end": v(-11.9, -4.76) * mm});
            skPoint(sketch, "E465.middle", {"position": v(-7.94, -7.94) * mm});
            skArc(sketch, "E466", {"start": v(-3.97, -4.76) * mm, "mid": v(-0.8, -7.94) * mm, "end": v(-3.97, -11.11) * mm});
            skArc(sketch, "E467", {"start": v(-11.9, -4.76) * mm, "mid": v(-15.08, -7.94) * mm, "end": v(-11.9, -11.11) * mm});
            skLineSegment(sketch, "E468.0.1.0", {"start": v(-3.97, -20.64) * mm, "end": v(-11.9, -20.64) * mm});
            skLineSegment(sketch, "E468.0.1.1", {"start": v(-3.97, -26.99) * mm, "end": v(-11.9, -26.99) * mm});
            skArc(sketch, "E468.0.1.2", {"start": v(-11.9, -20.64) * mm, "mid": v(-15.08, -23.81) * mm, "end": v(-11.9, -26.99) * mm});
            skArc(sketch, "E468.0.1.3", {"start": v(-3.97, -20.64) * mm, "mid": v(-0.8, -23.81) * mm, "end": v(-3.97, -26.99) * mm});
            skLineSegment(sketch, "E468.0.2.0", {"start": v(-3.97, -36.51) * mm, "end": v(-11.9, -36.51) * mm});
            skLineSegment(sketch, "E468.0.2.1", {"start": v(-3.97, -42.86) * mm, "end": v(-11.9, -42.86) * mm});
            skArc(sketch, "E468.0.2.2", {"start": v(-11.9, -36.51) * mm, "mid": v(-15.08, -39.69) * mm, "end": v(-11.9, -42.86) * mm});
            skArc(sketch, "E468.0.2.3", {"start": v(-3.97, -36.51) * mm, "mid": v(-0.8, -39.69) * mm, "end": v(-3.97, -42.86) * mm});
            skLineSegment(sketch, "E468.1.0.0", {"start": v(-19.84, -4.76) * mm, "end": v(-27.78, -4.76) * mm});
            skLineSegment(sketch, "E468.1.0.1", {"start": v(-19.84, -11.11) * mm, "end": v(-27.78, -11.11) * mm});
            skArc(sketch, "E468.1.0.2", {"start": v(-27.78, -4.76) * mm, "mid": v(-30.96, -7.94) * mm, "end": v(-27.78, -11.11) * mm});
            skArc(sketch, "E468.1.0.3", {"start": v(-19.84, -4.76) * mm, "mid": v(-16.67, -7.94) * mm, "end": v(-19.84, -11.11) * mm});
            skLineSegment(sketch, "E468.1.1.0", {"start": v(-19.84, -20.64) * mm, "end": v(-27.78, -20.64) * mm});
            skLineSegment(sketch, "E468.1.1.1", {"start": v(-19.84, -26.99) * mm, "end": v(-27.78, -26.99) * mm});
            skArc(sketch, "E468.1.1.2", {"start": v(-27.78, -20.64) * mm, "mid": v(-30.96, -23.81) * mm, "end": v(-27.78, -26.99) * mm});
            skArc(sketch, "E468.1.1.3", {"start": v(-19.84, -20.64) * mm, "mid": v(-16.67, -23.81) * mm, "end": v(-19.84, -26.99) * mm});
            skLineSegment(sketch, "E468.1.2.0", {"start": v(-19.84, -36.51) * mm, "end": v(-27.78, -36.51) * mm});
            skLineSegment(sketch, "E468.1.2.1", {"start": v(-19.84, -42.86) * mm, "end": v(-27.78, -42.86) * mm});
            skArc(sketch, "E468.1.2.2", {"start": v(-27.78, -36.51) * mm, "mid": v(-30.96, -39.69) * mm, "end": v(-27.78, -42.86) * mm});
            skArc(sketch, "E468.1.2.3", {"start": v(-19.84, -36.51) * mm, "mid": v(-16.67, -39.69) * mm, "end": v(-19.84, -42.86) * mm});
            skLineSegment(sketch, "E468.2.0.0", {"start": v(-35.72, -4.76) * mm, "end": v(-43.66, -4.76) * mm});
            skLineSegment(sketch, "E468.2.0.1", {"start": v(-35.72, -11.11) * mm, "end": v(-43.66, -11.11) * mm});
            skArc(sketch, "E468.2.0.2", {"start": v(-43.66, -4.76) * mm, "mid": v(-46.83, -7.94) * mm, "end": v(-43.66, -11.11) * mm});
            skArc(sketch, "E468.2.0.3", {"start": v(-35.72, -4.76) * mm, "mid": v(-32.54, -7.94) * mm, "end": v(-35.72, -11.11) * mm});
            skLineSegment(sketch, "E468.2.1.0", {"start": v(-35.72, -20.64) * mm, "end": v(-43.66, -20.64) * mm});
            skLineSegment(sketch, "E468.2.1.1", {"start": v(-35.72, -26.99) * mm, "end": v(-43.66, -26.99) * mm});
            skArc(sketch, "E468.2.1.2", {"start": v(-43.66, -20.64) * mm, "mid": v(-46.83, -23.81) * mm, "end": v(-43.66, -26.99) * mm});
            skArc(sketch, "E468.2.1.3", {"start": v(-35.72, -20.64) * mm, "mid": v(-32.54, -23.81) * mm, "end": v(-35.72, -26.99) * mm});
            skLineSegment(sketch, "E468.2.2.0", {"start": v(-35.72, -36.51) * mm, "end": v(-43.66, -36.51) * mm});
            skLineSegment(sketch, "E468.2.2.1", {"start": v(-35.72, -42.86) * mm, "end": v(-43.66, -42.86) * mm});
            skArc(sketch, "E468.2.2.2", {"start": v(-43.66, -36.51) * mm, "mid": v(-46.83, -39.69) * mm, "end": v(-43.66, -42.86) * mm});
            skArc(sketch, "E468.2.2.3", {"start": v(-35.72, -36.51) * mm, "mid": v(-32.54, -39.69) * mm, "end": v(-35.72, -42.86) * mm});
            skLineSegment(sketch, "E468.3.0.0", {"start": v(-51.6, -4.76) * mm, "end": v(-59.53, -4.76) * mm});
            skLineSegment(sketch, "E468.3.0.1", {"start": v(-51.6, -11.11) * mm, "end": v(-59.53, -11.11) * mm});
            skArc(sketch, "E468.3.0.2", {"start": v(-59.53, -4.76) * mm, "mid": v(-62.7, -7.94) * mm, "end": v(-59.53, -11.11) * mm});
            skArc(sketch, "E468.3.0.3", {"start": v(-51.6, -4.76) * mm, "mid": v(-48.42, -7.94) * mm, "end": v(-51.6, -11.11) * mm});
            skLineSegment(sketch, "E468.3.1.0", {"start": v(-51.6, -20.64) * mm, "end": v(-59.53, -20.64) * mm});
            skLineSegment(sketch, "E468.3.1.1", {"start": v(-51.6, -26.99) * mm, "end": v(-59.53, -26.99) * mm});
            skArc(sketch, "E468.3.1.2", {"start": v(-59.53, -20.64) * mm, "mid": v(-62.7, -23.81) * mm, "end": v(-59.53, -26.99) * mm});
            skArc(sketch, "E468.3.1.3", {"start": v(-51.6, -20.64) * mm, "mid": v(-48.42, -23.81) * mm, "end": v(-51.6, -26.99) * mm});
            skLineSegment(sketch, "E468.3.2.0", {"start": v(-51.6, -36.51) * mm, "end": v(-59.53, -36.51) * mm});
            skLineSegment(sketch, "E468.3.2.1", {"start": v(-51.6, -42.86) * mm, "end": v(-59.53, -42.86) * mm});
            skArc(sketch, "E468.3.2.2", {"start": v(-59.53, -36.51) * mm, "mid": v(-62.7, -39.69) * mm, "end": v(-59.53, -42.86) * mm});
            skArc(sketch, "E468.3.2.3", {"start": v(-51.6, -36.51) * mm, "mid": v(-48.42, -39.69) * mm, "end": v(-51.6, -42.86) * mm});
            skLineSegment(sketch, "E468.4.0.0", {"start": v(-67.47, -4.76) * mm, "end": v(-75.4, -4.76) * mm});
            skLineSegment(sketch, "E468.4.0.1", {"start": v(-67.47, -11.11) * mm, "end": v(-75.4, -11.11) * mm});
            skArc(sketch, "E468.4.0.2", {"start": v(-75.4, -4.76) * mm, "mid": v(-78.58, -7.94) * mm, "end": v(-75.4, -11.11) * mm});
            skArc(sketch, "E468.4.0.3", {"start": v(-67.47, -4.76) * mm, "mid": v(-64.3, -7.94) * mm, "end": v(-67.47, -11.11) * mm});
            skLineSegment(sketch, "E468.4.1.0", {"start": v(-67.47, -20.64) * mm, "end": v(-75.4, -20.64) * mm});
            skLineSegment(sketch, "E468.4.1.1", {"start": v(-67.47, -26.99) * mm, "end": v(-75.4, -26.99) * mm});
            skArc(sketch, "E468.4.1.2", {"start": v(-75.4, -20.64) * mm, "mid": v(-78.58, -23.81) * mm, "end": v(-75.4, -26.99) * mm});
            skArc(sketch, "E468.4.1.3", {"start": v(-67.47, -20.64) * mm, "mid": v(-64.3, -23.81) * mm, "end": v(-67.47, -26.99) * mm});
            skLineSegment(sketch, "E468.4.2.0", {"start": v(-67.47, -36.51) * mm, "end": v(-75.4, -36.51) * mm});
            skLineSegment(sketch, "E468.4.2.1", {"start": v(-67.47, -42.86) * mm, "end": v(-75.4, -42.86) * mm});
            skArc(sketch, "E468.4.2.2", {"start": v(-75.4, -36.51) * mm, "mid": v(-78.58, -39.69) * mm, "end": v(-75.4, -42.86) * mm});
            skArc(sketch, "E468.4.2.3", {"start": v(-67.47, -36.51) * mm, "mid": v(-64.3, -39.69) * mm, "end": v(-67.47, -42.86) * mm});
            skLineSegment(sketch, "E468.5.0.0", {"start": v(-83.34, -4.76) * mm, "end": v(-91.28, -4.76) * mm});
            skLineSegment(sketch, "E468.5.0.1", {"start": v(-83.34, -11.11) * mm, "end": v(-91.28, -11.11) * mm});
            skArc(sketch, "E468.5.0.2", {"start": v(-91.28, -4.76) * mm, "mid": v(-94.46, -7.94) * mm, "end": v(-91.28, -11.11) * mm});
            skArc(sketch, "E468.5.0.3", {"start": v(-83.34, -4.76) * mm, "mid": v(-80.17, -7.94) * mm, "end": v(-83.34, -11.11) * mm});
            skLineSegment(sketch, "E468.5.1.0", {"start": v(-83.34, -20.64) * mm, "end": v(-91.28, -20.64) * mm});
            skLineSegment(sketch, "E468.5.1.1", {"start": v(-83.34, -26.99) * mm, "end": v(-91.28, -26.99) * mm});
            skArc(sketch, "E468.5.1.2", {"start": v(-91.28, -20.64) * mm, "mid": v(-94.46, -23.81) * mm, "end": v(-91.28, -26.99) * mm});
            skArc(sketch, "E468.5.1.3", {"start": v(-83.34, -20.64) * mm, "mid": v(-80.17, -23.81) * mm, "end": v(-83.34, -26.99) * mm});
            skLineSegment(sketch, "E468.5.2.0", {"start": v(-83.34, -36.51) * mm, "end": v(-91.28, -36.51) * mm});
            skLineSegment(sketch, "E468.5.2.1", {"start": v(-83.34, -42.86) * mm, "end": v(-91.28, -42.86) * mm});
            skArc(sketch, "E468.5.2.2", {"start": v(-91.28, -36.51) * mm, "mid": v(-94.46, -39.69) * mm, "end": v(-91.28, -42.86) * mm});
            skArc(sketch, "E468.5.2.3", {"start": v(-83.34, -36.51) * mm, "mid": v(-80.17, -39.69) * mm, "end": v(-83.34, -42.86) * mm});
            skLineSegment(sketch, "E468.direction1", {"start": v(-11.9, -4.76) * mm, "end": v(-27.78, -4.76) * mm, "construction": true});
            skLineSegment(sketch, "E468.direction2", {"start": v(-11.9, -11.11) * mm, "end": v(-11.9, -20.64) * mm, "construction": true});
            skLineSegment(sketch, "E469.MirrorCS", {"start": v(-19.84, 4.76) * mm, "end": v(-27.78, 4.76) * mm});
            skArc(sketch, "E470.MirrorCS", {"start": v(-51.6, 36.51) * mm, "mid": v(-48.42, 39.69) * mm, "end": v(-51.6, 42.86) * mm});
            skArc(sketch, "E471.MirrorCS", {"start": v(-59.53, 36.51) * mm, "mid": v(-62.7, 39.69) * mm, "end": v(-59.53, 42.86) * mm});
            skArc(sketch, "E472.MirrorCS", {"start": v(-11.9, 36.51) * mm, "mid": v(-15.08, 39.69) * mm, "end": v(-11.9, 42.86) * mm});
            skArc(sketch, "E473.MirrorCS", {"start": v(-75.4, 36.51) * mm, "mid": v(-78.58, 39.69) * mm, "end": v(-75.4, 42.86) * mm});
            skArc(sketch, "E474.MirrorCS", {"start": v(-67.47, 36.51) * mm, "mid": v(-64.3, 39.69) * mm, "end": v(-67.47, 42.86) * mm});
            skArc(sketch, "E475.MirrorCS", {"start": v(-35.72, 4.76) * mm, "mid": v(-32.54, 7.94) * mm, "end": v(-35.72, 11.11) * mm});
            skLineSegment(sketch, "E476.MirrorCS", {"start": v(-67.47, 26.99) * mm, "end": v(-75.4, 26.99) * mm});
            skLineSegment(sketch, "E477.MirrorCS", {"start": v(-3.97, 26.99) * mm, "end": v(-11.9, 26.99) * mm});
            skLineSegment(sketch, "E478.MirrorCS", {"start": v(-51.6, 42.86) * mm, "end": v(-59.53, 42.86) * mm});
            skLineSegment(sketch, "E479.MirrorCS", {"start": v(-19.84, 11.11) * mm, "end": v(-27.78, 11.11) * mm});
            skLineSegment(sketch, "E480.MirrorCS", {"start": v(-19.84, 36.51) * mm, "end": v(-27.78, 36.51) * mm});
            skLineSegment(sketch, "E481.MirrorCS", {"start": v(-67.47, 20.64) * mm, "end": v(-75.4, 20.64) * mm});
            skArc(sketch, "E482.MirrorCS", {"start": v(-19.84, 36.51) * mm, "mid": v(-16.67, 39.69) * mm, "end": v(-19.84, 42.86) * mm});
            skArc(sketch, "E483.MirrorCS", {"start": v(-51.6, 4.76) * mm, "mid": v(-48.42, 7.94) * mm, "end": v(-51.6, 11.11) * mm});
            skArc(sketch, "E484.MirrorCS", {"start": v(-83.34, 36.51) * mm, "mid": v(-80.17, 39.69) * mm, "end": v(-83.34, 42.86) * mm});
            skArc(sketch, "E485.MirrorCS", {"start": v(-27.78, 4.76) * mm, "mid": v(-30.96, 7.94) * mm, "end": v(-27.78, 11.11) * mm});
            skArc(sketch, "E486.MirrorCS", {"start": v(-11.9, 4.76) * mm, "mid": v(-15.08, 7.94) * mm, "end": v(-11.9, 11.11) * mm});
            skArc(sketch, "E487.MirrorCS", {"start": v(-3.97, 4.76) * mm, "mid": v(-0.8, 7.94) * mm, "end": v(-3.97, 11.11) * mm});
            skLineSegment(sketch, "E488.MirrorCS", {"start": v(-35.72, 11.11) * mm, "end": v(-43.66, 11.11) * mm});
            skLineSegment(sketch, "E489.MirrorCS", {"start": v(-83.34, 20.64) * mm, "end": v(-91.28, 20.64) * mm});
            skArc(sketch, "E490.MirrorCS", {"start": v(-19.84, 4.76) * mm, "mid": v(-16.67, 7.94) * mm, "end": v(-19.84, 11.11) * mm});
            skLineSegment(sketch, "E491.MirrorCS", {"start": v(-11.9, 11.11) * mm, "end": v(-11.9, 20.64) * mm, "construction": true});
            skLineSegment(sketch, "E492.MirrorCS", {"start": v(-3.97, 36.51) * mm, "end": v(-11.9, 36.51) * mm});
            skLineSegment(sketch, "E493.MirrorCS", {"start": v(-35.72, 4.76) * mm, "end": v(-43.66, 4.76) * mm});
            skArc(sketch, "E494.MirrorCS", {"start": v(-35.72, 36.51) * mm, "mid": v(-32.54, 39.69) * mm, "end": v(-35.72, 42.86) * mm});
            skLineSegment(sketch, "E495.MirrorCS", {"start": v(-83.34, 4.76) * mm, "end": v(-91.28, 4.76) * mm});
            skLineSegment(sketch, "E496.MirrorCS", {"start": v(-51.6, 36.51) * mm, "end": v(-59.53, 36.51) * mm});
            skLineSegment(sketch, "E497.MirrorCS", {"start": v(-51.6, 11.11) * mm, "end": v(-59.53, 11.11) * mm});
            skLineSegment(sketch, "E498.MirrorCS", {"start": v(-51.6, 26.99) * mm, "end": v(-59.53, 26.99) * mm});
            skLineSegment(sketch, "E499.MirrorCS", {"start": v(-3.97, 4.76) * mm, "end": v(-11.9, 4.76) * mm});
            skLineSegment(sketch, "E500.MirrorCS", {"start": v(-67.47, 11.11) * mm, "end": v(-75.4, 11.11) * mm});
            skArc(sketch, "E501.MirrorCS", {"start": v(-11.9, 20.64) * mm, "mid": v(-15.08, 23.81) * mm, "end": v(-11.9, 26.99) * mm});
            skArc(sketch, "E502.MirrorCS", {"start": v(-75.4, 20.64) * mm, "mid": v(-78.58, 23.81) * mm, "end": v(-75.4, 26.99) * mm});
            skArc(sketch, "E503.MirrorCS", {"start": v(-91.28, 20.64) * mm, "mid": v(-94.46, 23.81) * mm, "end": v(-91.28, 26.99) * mm});
            skArc(sketch, "E504.MirrorCS", {"start": v(-59.53, 4.76) * mm, "mid": v(-62.7, 7.94) * mm, "end": v(-59.53, 11.11) * mm});
            skLineSegment(sketch, "E505.MirrorCS", {"start": v(-51.6, 20.64) * mm, "end": v(-59.53, 20.64) * mm});
            skLineSegment(sketch, "E506.MirrorCS", {"start": v(-19.84, 42.86) * mm, "end": v(-27.78, 42.86) * mm});
            skArc(sketch, "E507.MirrorCS", {"start": v(-83.34, 4.76) * mm, "mid": v(-80.17, 7.94) * mm, "end": v(-83.34, 11.11) * mm});
            skLineSegment(sketch, "E508.MirrorCS", {"start": v(-19.84, 20.64) * mm, "end": v(-27.78, 20.64) * mm});
            skLineSegment(sketch, "E509.MirrorCS", {"start": v(-67.47, 36.51) * mm, "end": v(-75.4, 36.51) * mm});
            skArc(sketch, "E510.MirrorCS", {"start": v(-43.66, 4.76) * mm, "mid": v(-46.83, 7.94) * mm, "end": v(-43.66, 11.11) * mm});
            skArc(sketch, "E511.MirrorCS", {"start": v(-59.53, 20.64) * mm, "mid": v(-62.7, 23.81) * mm, "end": v(-59.53, 26.99) * mm});
            skLineSegment(sketch, "E512.MirrorCS", {"start": v(-35.72, 36.51) * mm, "end": v(-43.66, 36.51) * mm});
            skLineSegment(sketch, "E513.MirrorCS", {"start": v(-67.47, 4.76) * mm, "end": v(-75.4, 4.76) * mm});
            skPoint(sketch, "E514.MirrorP", {"position": v(-7.94, 7.94) * mm});
            skArc(sketch, "E515.MirrorCS", {"start": v(-67.47, 20.64) * mm, "mid": v(-64.3, 23.81) * mm, "end": v(-67.47, 26.99) * mm});
            skLineSegment(sketch, "E516.MirrorCS", {"start": v(-51.6, 4.76) * mm, "end": v(-59.53, 4.76) * mm});
            skArc(sketch, "E517.MirrorCS", {"start": v(-43.66, 20.64) * mm, "mid": v(-46.83, 23.81) * mm, "end": v(-43.66, 26.99) * mm});
            skLineSegment(sketch, "E518.MirrorCS", {"start": v(-83.34, 36.51) * mm, "end": v(-91.28, 36.51) * mm});
            skLineSegment(sketch, "E519.MirrorCS", {"start": v(-83.34, 42.86) * mm, "end": v(-91.28, 42.86) * mm});
            skLineSegment(sketch, "E520.MirrorCS", {"start": v(-67.47, 42.86) * mm, "end": v(-75.4, 42.86) * mm});
            skArc(sketch, "E521.MirrorCS", {"start": v(-27.78, 20.64) * mm, "mid": v(-30.96, 23.81) * mm, "end": v(-27.78, 26.99) * mm});
            skLineSegment(sketch, "E522.MirrorCS", {"start": v(-3.97, 42.86) * mm, "end": v(-11.9, 42.86) * mm});
            skLineSegment(sketch, "E523.MirrorCS", {"start": v(-83.34, 26.99) * mm, "end": v(-91.28, 26.99) * mm});
            skArc(sketch, "E524.MirrorCS", {"start": v(-91.28, 36.51) * mm, "mid": v(-94.46, 39.69) * mm, "end": v(-91.28, 42.86) * mm});
            skArc(sketch, "E525.MirrorCS", {"start": v(-3.97, 36.51) * mm, "mid": v(-0.8, 39.69) * mm, "end": v(-3.97, 42.86) * mm});
            skArc(sketch, "E526.MirrorCS", {"start": v(-35.72, 20.64) * mm, "mid": v(-32.54, 23.81) * mm, "end": v(-35.72, 26.99) * mm});
            skArc(sketch, "E527.MirrorCS", {"start": v(-67.47, 4.76) * mm, "mid": v(-64.3, 7.94) * mm, "end": v(-67.47, 11.11) * mm});
            skArc(sketch, "E528.MirrorCS", {"start": v(-19.84, 20.64) * mm, "mid": v(-16.67, 23.81) * mm, "end": v(-19.84, 26.99) * mm});
            skArc(sketch, "E529.MirrorCS", {"start": v(-83.34, 20.64) * mm, "mid": v(-80.17, 23.81) * mm, "end": v(-83.34, 26.99) * mm});
            skArc(sketch, "E530.MirrorCS", {"start": v(-27.78, 36.51) * mm, "mid": v(-30.96, 39.69) * mm, "end": v(-27.78, 42.86) * mm});
            skArc(sketch, "E531.MirrorCS", {"start": v(-43.66, 36.51) * mm, "mid": v(-46.83, 39.69) * mm, "end": v(-43.66, 42.86) * mm});
            skLineSegment(sketch, "E532.MirrorCS", {"start": v(-3.97, 20.64) * mm, "end": v(-11.9, 20.64) * mm});
            skLineSegment(sketch, "E533.MirrorCS", {"start": v(-83.34, 11.11) * mm, "end": v(-91.28, 11.11) * mm});
            skArc(sketch, "E534.MirrorCS", {"start": v(-75.4, 4.76) * mm, "mid": v(-78.58, 7.94) * mm, "end": v(-75.4, 11.11) * mm});
            skLineSegment(sketch, "E535.MirrorCS", {"start": v(-3.97, 11.11) * mm, "end": v(-11.9, 11.11) * mm});
            skLineSegment(sketch, "E536.MirrorCS", {"start": v(-35.72, 26.99) * mm, "end": v(-43.66, 26.99) * mm});
            skLineSegment(sketch, "E537.MirrorCS", {"start": v(-35.72, 42.86) * mm, "end": v(-43.66, 42.86) * mm});
            skLineSegment(sketch, "E538.MirrorCS", {"start": v(-19.84, 26.99) * mm, "end": v(-27.78, 26.99) * mm});
            skArc(sketch, "E539.MirrorCS", {"start": v(-51.6, 20.64) * mm, "mid": v(-48.42, 23.81) * mm, "end": v(-51.6, 26.99) * mm});
            skLineSegment(sketch, "E540.MirrorCS", {"start": v(-35.72, 20.64) * mm, "end": v(-43.66, 20.64) * mm});
            skArc(sketch, "E541.MirrorCS", {"start": v(-3.97, 20.64) * mm, "mid": v(-0.8, 23.81) * mm, "end": v(-3.97, 26.99) * mm});
            skArc(sketch, "E542.MirrorCS", {"start": v(-91.28, 4.76) * mm, "mid": v(-94.46, 7.94) * mm, "end": v(-91.28, 11.11) * mm});
            skLineSegment(sketch, "E543.MirrorCS", {"start": v(-11.9, 4.76) * mm, "end": v(-27.78, 4.76) * mm, "construction": true});
            skLineSegment(sketch, "E544.MirrorCS", {"start": v(19.84, 4.76) * mm, "end": v(27.78, 4.76) * mm});
            skLineSegment(sketch, "E545.MirrorCS", {"start": v(3.97, -4.76) * mm, "end": v(11.9, -4.76) * mm});
            skLineSegment(sketch, "E546.MirrorCS", {"start": v(19.84, -4.76) * mm, "end": v(27.78, -4.76) * mm});
            skLineSegment(sketch, "E547.MirrorCS", {"start": v(7.94, 0) * mm, "end": v(7.94, -7.94) * mm});
            skLineSegment(sketch, "E548.MirrorCS", {"start": v(35.72, 11.11) * mm, "end": v(43.66, 11.11) * mm});
            skArc(sketch, "E549.MirrorCS", {"start": v(59.53, 4.76) * mm, "mid": v(62.7, 7.94) * mm, "end": v(59.53, 11.11) * mm});
            skLineSegment(sketch, "E550.MirrorCS", {"start": v(51.6, -36.51) * mm, "end": v(59.53, -36.51) * mm});
            skArc(sketch, "E551.MirrorCS", {"start": v(59.53, 36.51) * mm, "mid": v(62.7, 39.69) * mm, "end": v(59.53, 42.86) * mm});
            skArc(sketch, "E552.MirrorCS", {"start": v(3.97, 4.76) * mm, "mid": v(0.8, 7.94) * mm, "end": v(3.97, 11.11) * mm});
            skArc(sketch, "E553.MirrorCS", {"start": v(91.28, 20.64) * mm, "mid": v(94.46, 23.81) * mm, "end": v(91.28, 26.99) * mm});
            skLineSegment(sketch, "E554.MirrorCS", {"start": v(67.47, 42.86) * mm, "end": v(75.4, 42.86) * mm});
            skLineSegment(sketch, "E555.MirrorCS", {"start": v(35.72, 26.99) * mm, "end": v(43.66, 26.99) * mm});
            skArc(sketch, "E556.MirrorCS", {"start": v(3.97, -36.51) * mm, "mid": v(0.8, -39.69) * mm, "end": v(3.97, -42.86) * mm});
            skArc(sketch, "E557.MirrorCS", {"start": v(75.4, 20.64) * mm, "mid": v(78.58, 23.81) * mm, "end": v(75.4, 26.99) * mm});
            skLineSegment(sketch, "E558.MirrorCS", {"start": v(83.34, 42.86) * mm, "end": v(91.28, 42.86) * mm});
            skArc(sketch, "E559.MirrorCS", {"start": v(35.72, -4.76) * mm, "mid": v(32.54, -7.94) * mm, "end": v(35.72, -11.11) * mm});
            skArc(sketch, "E560.MirrorCS", {"start": v(51.6, 36.51) * mm, "mid": v(48.42, 39.69) * mm, "end": v(51.6, 42.86) * mm});
            skArc(sketch, "E561.MirrorCS", {"start": v(27.78, 4.76) * mm, "mid": v(30.96, 7.94) * mm, "end": v(27.78, 11.11) * mm});
            skArc(sketch, "E562.MirrorCS", {"start": v(11.9, 20.64) * mm, "mid": v(15.08, 23.81) * mm, "end": v(11.9, 26.99) * mm});
            skLineSegment(sketch, "E563.MirrorCS", {"start": v(83.34, 36.51) * mm, "end": v(91.28, 36.51) * mm});
            skArc(sketch, "E564.MirrorCS", {"start": v(75.4, 4.76) * mm, "mid": v(78.58, 7.94) * mm, "end": v(75.4, 11.11) * mm});
            skArc(sketch, "E565.MirrorCS", {"start": v(43.66, -4.76) * mm, "mid": v(46.83, -7.94) * mm, "end": v(43.66, -11.11) * mm});
            skArc(sketch, "E566.MirrorCS", {"start": v(59.53, -20.64) * mm, "mid": v(62.7, -23.81) * mm, "end": v(59.53, -26.99) * mm});
            skArc(sketch, "E567.MirrorCS", {"start": v(75.4, -36.51) * mm, "mid": v(78.58, -39.69) * mm, "end": v(75.4, -42.86) * mm});
            skArc(sketch, "E568.MirrorCS", {"start": v(11.9, -36.51) * mm, "mid": v(15.08, -39.69) * mm, "end": v(11.9, -42.86) * mm});
            skArc(sketch, "E569.MirrorCS", {"start": v(83.34, 36.51) * mm, "mid": v(80.17, 39.69) * mm, "end": v(83.34, 42.86) * mm});
            skLineSegment(sketch, "E570.MirrorCS", {"start": v(67.47, 11.11) * mm, "end": v(75.4, 11.11) * mm});
            skArc(sketch, "E571.MirrorCS", {"start": v(43.66, 20.64) * mm, "mid": v(46.83, 23.81) * mm, "end": v(43.66, 26.99) * mm});
            skLineSegment(sketch, "E572.MirrorCS", {"start": v(83.34, 11.11) * mm, "end": v(91.28, 11.11) * mm});
            skLineSegment(sketch, "E573.MirrorCS", {"start": v(35.72, -11.11) * mm, "end": v(43.66, -11.11) * mm});
            skLineSegment(sketch, "E574.MirrorCS", {"start": v(51.6, -26.99) * mm, "end": v(59.53, -26.99) * mm});
            skLineSegment(sketch, "E575.MirrorCS", {"start": v(67.47, -42.86) * mm, "end": v(75.4, -42.86) * mm});
            skLineSegment(sketch, "E576.MirrorCS", {"start": v(11.9, -11.11) * mm, "end": v(11.9, -20.64) * mm, "construction": true});
            skPoint(sketch, "E577.MirrorP", {"position": v(7.94, 7.94) * mm});
            skArc(sketch, "E578.MirrorCS", {"start": v(51.6, 4.76) * mm, "mid": v(48.42, 7.94) * mm, "end": v(51.6, 11.11) * mm});
            skLineSegment(sketch, "E579.MirrorCS", {"start": v(3.97, 4.76) * mm, "end": v(11.9, 4.76) * mm});
            skLineSegment(sketch, "E580.MirrorCS", {"start": v(51.6, 4.76) * mm, "end": v(59.53, 4.76) * mm});
            skLineSegment(sketch, "E581.MirrorCS", {"start": v(3.97, 20.64) * mm, "end": v(11.9, 20.64) * mm});
            skLineSegment(sketch, "E582.MirrorCS", {"start": v(35.72, -4.76) * mm, "end": v(43.66, -4.76) * mm});
            skLineSegment(sketch, "E583.MirrorCS", {"start": v(51.6, -20.64) * mm, "end": v(59.53, -20.64) * mm});
            skLineSegment(sketch, "E584.MirrorCS", {"start": v(67.47, -36.51) * mm, "end": v(75.4, -36.51) * mm});
            skLineSegment(sketch, "E585.MirrorCS", {"start": v(11.9, -4.76) * mm, "end": v(27.78, -4.76) * mm, "construction": true});
            skArc(sketch, "E586.MirrorCS", {"start": v(27.78, 36.51) * mm, "mid": v(30.96, 39.69) * mm, "end": v(27.78, 42.86) * mm});
            skArc(sketch, "E587.MirrorCS", {"start": v(91.28, -36.51) * mm, "mid": v(94.46, -39.69) * mm, "end": v(91.28, -42.86) * mm});
            skLineSegment(sketch, "E588.MirrorCS", {"start": v(67.47, 20.64) * mm, "end": v(75.4, 20.64) * mm});
            skLineSegment(sketch, "E589.MirrorCS", {"start": v(51.6, 11.11) * mm, "end": v(59.53, 11.11) * mm});
            skLineSegment(sketch, "E590.MirrorCS", {"start": v(67.47, 4.76) * mm, "end": v(75.4, 4.76) * mm});
            skArc(sketch, "E591.MirrorCS", {"start": v(27.78, -36.51) * mm, "mid": v(30.96, -39.69) * mm, "end": v(27.78, -42.86) * mm});
            skArc(sketch, "E592.MirrorCS", {"start": v(59.53, -4.76) * mm, "mid": v(62.7, -7.94) * mm, "end": v(59.53, -11.11) * mm});
            skArc(sketch, "E593.MirrorCS", {"start": v(75.4, -20.64) * mm, "mid": v(78.58, -23.81) * mm, "end": v(75.4, -26.99) * mm});
            skArc(sketch, "E594.MirrorCS", {"start": v(19.84, 36.51) * mm, "mid": v(16.67, 39.69) * mm, "end": v(19.84, 42.86) * mm});
            skLineSegment(sketch, "E595.MirrorCS", {"start": v(51.6, 26.99) * mm, "end": v(59.53, 26.99) * mm});
            skArc(sketch, "E596.MirrorCS", {"start": v(67.47, 20.64) * mm, "mid": v(64.3, 23.81) * mm, "end": v(67.47, 26.99) * mm});
            skArc(sketch, "E597.MirrorCS", {"start": v(43.66, 36.51) * mm, "mid": v(46.83, 39.69) * mm, "end": v(43.66, 42.86) * mm});
            skArc(sketch, "E598.MirrorCS", {"start": v(19.84, -36.51) * mm, "mid": v(16.67, -39.69) * mm, "end": v(19.84, -42.86) * mm});
            skArc(sketch, "E599.MirrorCS", {"start": v(67.47, -20.64) * mm, "mid": v(64.3, -23.81) * mm, "end": v(67.47, -26.99) * mm});
            skArc(sketch, "E600.MirrorCS", {"start": v(83.34, -36.51) * mm, "mid": v(80.17, -39.69) * mm, "end": v(83.34, -42.86) * mm});
            skArc(sketch, "E601.MirrorCS", {"start": v(83.34, 20.64) * mm, "mid": v(80.17, 23.81) * mm, "end": v(83.34, 26.99) * mm});
            skLineSegment(sketch, "E602.MirrorCS", {"start": v(83.34, -42.86) * mm, "end": v(91.28, -42.86) * mm});
            skLineSegment(sketch, "E603.MirrorCS", {"start": v(19.84, 36.51) * mm, "end": v(27.78, 36.51) * mm});
            skLineSegment(sketch, "E604.MirrorCS", {"start": v(51.6, 36.51) * mm, "end": v(59.53, 36.51) * mm});
            skLineSegment(sketch, "E605.MirrorCS", {"start": v(35.72, 36.51) * mm, "end": v(43.66, 36.51) * mm});
            skLineSegment(sketch, "E606.MirrorCS", {"start": v(19.84, -42.86) * mm, "end": v(27.78, -42.86) * mm});
            skLineSegment(sketch, "E607.MirrorCS", {"start": v(51.6, -11.11) * mm, "end": v(59.53, -11.11) * mm});
            skLineSegment(sketch, "E608.MirrorCS", {"start": v(67.47, -26.99) * mm, "end": v(75.4, -26.99) * mm});
            skArc(sketch, "E609.MirrorCS", {"start": v(19.84, 20.64) * mm, "mid": v(16.67, 23.81) * mm, "end": v(19.84, 26.99) * mm});
            skLineSegment(sketch, "E610.MirrorCS", {"start": v(83.34, -36.51) * mm, "end": v(91.28, -36.51) * mm});
            skLineSegment(sketch, "E611.MirrorCS", {"start": v(19.84, 11.11) * mm, "end": v(27.78, 11.11) * mm});
            skLineSegment(sketch, "E612.MirrorCS", {"start": v(83.34, 4.76) * mm, "end": v(91.28, 4.76) * mm});
            skLineSegment(sketch, "E613.MirrorCS", {"start": v(19.84, -36.51) * mm, "end": v(27.78, -36.51) * mm});
            skLineSegment(sketch, "E614.MirrorCS", {"start": v(51.6, -4.76) * mm, "end": v(59.53, -4.76) * mm});
            skLineSegment(sketch, "E615.MirrorCS", {"start": v(67.47, -20.64) * mm, "end": v(75.4, -20.64) * mm});
            skLineSegment(sketch, "E616.MirrorCS", {"start": v(35.72, 4.76) * mm, "end": v(43.66, 4.76) * mm});
            skArc(sketch, "E617.MirrorCS", {"start": v(11.9, -4.76) * mm, "mid": v(15.08, -7.94) * mm, "end": v(11.9, -11.11) * mm});
            skLineSegment(sketch, "E618.MirrorCS", {"start": v(35.72, 42.86) * mm, "end": v(43.66, 42.86) * mm});
            skLineSegment(sketch, "E619.MirrorCS", {"start": v(35.72, -20.64) * mm, "end": v(43.66, -20.64) * mm});
            skArc(sketch, "E620.MirrorCS", {"start": v(35.72, 36.51) * mm, "mid": v(32.54, 39.69) * mm, "end": v(35.72, 42.86) * mm});
            skLineSegment(sketch, "E621.MirrorCS", {"start": v(3.97, -42.86) * mm, "end": v(11.9, -42.86) * mm});
            skArc(sketch, "E622.MirrorCS", {"start": v(67.47, -4.76) * mm, "mid": v(64.3, -7.94) * mm, "end": v(67.47, -11.11) * mm});
            skLineSegment(sketch, "E623.MirrorCS", {"start": v(3.97, -20.64) * mm, "end": v(11.9, -20.64) * mm});
            skLineSegment(sketch, "E624.MirrorCS", {"start": v(3.97, -26.99) * mm, "end": v(11.9, -26.99) * mm});
            skLineSegment(sketch, "E625.MirrorCS", {"start": v(3.97, 11.11) * mm, "end": v(11.9, 11.11) * mm});
            skArc(sketch, "E626.MirrorCS", {"start": v(3.97, -20.64) * mm, "mid": v(0.8, -23.81) * mm, "end": v(3.97, -26.99) * mm});
            skLineSegment(sketch, "E627.MirrorCS", {"start": v(51.6, 42.86) * mm, "end": v(59.53, 42.86) * mm});
            skArc(sketch, "E628.MirrorCS", {"start": v(11.9, 36.51) * mm, "mid": v(15.08, 39.69) * mm, "end": v(11.9, 42.86) * mm});
            skArc(sketch, "E629.MirrorCS", {"start": v(67.47, 36.51) * mm, "mid": v(64.3, 39.69) * mm, "end": v(67.47, 42.86) * mm});
            skArc(sketch, "E630.MirrorCS", {"start": v(35.72, -36.51) * mm, "mid": v(32.54, -39.69) * mm, "end": v(35.72, -42.86) * mm});
            skArc(sketch, "E631.MirrorCS", {"start": v(19.84, -20.64) * mm, "mid": v(16.67, -23.81) * mm, "end": v(19.84, -26.99) * mm});
            skArc(sketch, "E632.MirrorCS", {"start": v(11.9, -20.64) * mm, "mid": v(15.08, -23.81) * mm, "end": v(11.9, -26.99) * mm});
            skArc(sketch, "E633.MirrorCS", {"start": v(59.53, 20.64) * mm, "mid": v(62.7, 23.81) * mm, "end": v(59.53, 26.99) * mm});
            skLineSegment(sketch, "E634.MirrorCS", {"start": v(51.6, 20.64) * mm, "end": v(59.53, 20.64) * mm});
            skLineSegment(sketch, "E635.MirrorCS", {"start": v(83.34, 20.64) * mm, "end": v(91.28, 20.64) * mm});
            skLineSegment(sketch, "E636.MirrorCS", {"start": v(83.34, 26.99) * mm, "end": v(91.28, 26.99) * mm});
            skLineSegment(sketch, "E637.MirrorCS", {"start": v(67.47, -11.11) * mm, "end": v(75.4, -11.11) * mm});
            skArc(sketch, "E638.MirrorCS", {"start": v(3.97, 36.51) * mm, "mid": v(0.8, 39.69) * mm, "end": v(3.97, 42.86) * mm});
            skLineSegment(sketch, "E639.MirrorCS", {"start": v(83.34, -26.99) * mm, "end": v(91.28, -26.99) * mm});
            skLineSegment(sketch, "E640.MirrorCS", {"start": v(3.97, -11.11) * mm, "end": v(11.9, -11.11) * mm});
            skArc(sketch, "E641.MirrorCS", {"start": v(27.78, -4.76) * mm, "mid": v(30.96, -7.94) * mm, "end": v(27.78, -11.11) * mm});
            skLineSegment(sketch, "E642.MirrorCS", {"start": v(19.84, 42.86) * mm, "end": v(27.78, 42.86) * mm});
            skLineSegment(sketch, "E643.MirrorCS", {"start": v(35.72, -36.51) * mm, "end": v(43.66, -36.51) * mm});
            skLineSegment(sketch, "E644.MirrorCS", {"start": v(35.72, -26.99) * mm, "end": v(43.66, -26.99) * mm});
            skLineSegment(sketch, "E645.MirrorCS", {"start": v(67.47, 26.99) * mm, "end": v(75.4, 26.99) * mm});
            skLineSegment(sketch, "E646.MirrorCS", {"start": v(3.97, 36.51) * mm, "end": v(11.9, 36.51) * mm});
            skArc(sketch, "E647.MirrorCS", {"start": v(91.28, 36.51) * mm, "mid": v(94.46, 39.69) * mm, "end": v(91.28, 42.86) * mm});
            skArc(sketch, "E648.MirrorCS", {"start": v(75.4, 36.51) * mm, "mid": v(78.58, 39.69) * mm, "end": v(75.4, 42.86) * mm});
            skArc(sketch, "E649.MirrorCS", {"start": v(83.34, 4.76) * mm, "mid": v(80.17, 7.94) * mm, "end": v(83.34, 11.11) * mm});
            skArc(sketch, "E650.MirrorCS", {"start": v(83.34, -4.76) * mm, "mid": v(80.17, -7.94) * mm, "end": v(83.34, -11.11) * mm});
            skArc(sketch, "E651.MirrorCS", {"start": v(51.6, -36.51) * mm, "mid": v(48.42, -39.69) * mm, "end": v(51.6, -42.86) * mm});
            skArc(sketch, "E652.MirrorCS", {"start": v(67.47, 4.76) * mm, "mid": v(64.3, 7.94) * mm, "end": v(67.47, 11.11) * mm});
            skArc(sketch, "E653.MirrorCS", {"start": v(51.6, -20.64) * mm, "mid": v(48.42, -23.81) * mm, "end": v(51.6, -26.99) * mm});
            skArc(sketch, "E654.MirrorCS", {"start": v(91.28, 4.76) * mm, "mid": v(94.46, 7.94) * mm, "end": v(91.28, 11.11) * mm});
            skLineSegment(sketch, "E655.MirrorCS", {"start": v(11.9, 4.76) * mm, "end": v(27.78, 4.76) * mm, "construction": true});
            skLineSegment(sketch, "E656.MirrorCS", {"start": v(67.47, 36.51) * mm, "end": v(75.4, 36.51) * mm});
            skArc(sketch, "E657.MirrorCS", {"start": v(19.84, -4.76) * mm, "mid": v(16.67, -7.94) * mm, "end": v(19.84, -11.11) * mm});
            skArc(sketch, "E658.MirrorCS", {"start": v(91.28, -20.64) * mm, "mid": v(94.46, -23.81) * mm, "end": v(91.28, -26.99) * mm});
            skArc(sketch, "E659.MirrorCS", {"start": v(3.97, -4.76) * mm, "mid": v(0.8, -7.94) * mm, "end": v(3.97, -11.11) * mm});
            skLineSegment(sketch, "E660.MirrorCS", {"start": v(19.84, 20.64) * mm, "end": v(27.78, 20.64) * mm});
            skArc(sketch, "E661.MirrorCS", {"start": v(19.84, 4.76) * mm, "mid": v(16.67, 7.94) * mm, "end": v(19.84, 11.11) * mm});
            skLineSegment(sketch, "E662.MirrorCS", {"start": v(3.97, 42.86) * mm, "end": v(11.9, 42.86) * mm});
            skLineSegment(sketch, "E663.MirrorCS", {"start": v(3.97, 26.99) * mm, "end": v(11.9, 26.99) * mm});
            skArc(sketch, "E664.MirrorCS", {"start": v(83.34, -20.64) * mm, "mid": v(80.17, -23.81) * mm, "end": v(83.34, -26.99) * mm});
            skArc(sketch, "E665.MirrorCS", {"start": v(75.4, -4.76) * mm, "mid": v(78.58, -7.94) * mm, "end": v(75.4, -11.11) * mm});
            skArc(sketch, "E666.MirrorCS", {"start": v(27.78, -20.64) * mm, "mid": v(30.96, -23.81) * mm, "end": v(27.78, -26.99) * mm});
            skArc(sketch, "E667.MirrorCS", {"start": v(51.6, -4.76) * mm, "mid": v(48.42, -7.94) * mm, "end": v(51.6, -11.11) * mm});
            skLineSegment(sketch, "E668.MirrorCS", {"start": v(67.47, -4.76) * mm, "end": v(75.4, -4.76) * mm});
            skLineSegment(sketch, "E669.MirrorCS", {"start": v(11.9, 11.11) * mm, "end": v(11.9, 20.64) * mm, "construction": true});
            skLineSegment(sketch, "E670.MirrorCS", {"start": v(83.34, -20.64) * mm, "end": v(91.28, -20.64) * mm});
            skArc(sketch, "E671.MirrorCS", {"start": v(35.72, 4.76) * mm, "mid": v(32.54, 7.94) * mm, "end": v(35.72, 11.11) * mm});
            skLineSegment(sketch, "E672.MirrorCS", {"start": v(19.84, -20.64) * mm, "end": v(27.78, -20.64) * mm});
            skArc(sketch, "E673.MirrorCS", {"start": v(91.28, -4.76) * mm, "mid": v(94.46, -7.94) * mm, "end": v(91.28, -11.11) * mm});
            skLineSegment(sketch, "E674.MirrorCS", {"start": v(19.84, -26.99) * mm, "end": v(27.78, -26.99) * mm});
            skLineSegment(sketch, "E675.MirrorCS", {"start": v(35.72, 20.64) * mm, "end": v(43.66, 20.64) * mm});
            skLineSegment(sketch, "E676.MirrorCS", {"start": v(3.97, -36.51) * mm, "end": v(11.9, -36.51) * mm});
            skLineSegment(sketch, "E677.MirrorCS", {"start": v(35.72, -42.86) * mm, "end": v(43.66, -42.86) * mm});
            skArc(sketch, "E678.MirrorCS", {"start": v(27.78, 20.64) * mm, "mid": v(30.96, 23.81) * mm, "end": v(27.78, 26.99) * mm});
            skLineSegment(sketch, "E679.MirrorCS", {"start": v(19.84, -11.11) * mm, "end": v(27.78, -11.11) * mm});
            skLineSegment(sketch, "E680.MirrorCS", {"start": v(0, 0) * mm, "end": v(7.94, 0) * mm});
            skArc(sketch, "E681.MirrorCS", {"start": v(3.97, 20.64) * mm, "mid": v(0.8, 23.81) * mm, "end": v(3.97, 26.99) * mm});
            skArc(sketch, "E682.MirrorCS", {"start": v(59.53, -36.51) * mm, "mid": v(62.7, -39.69) * mm, "end": v(59.53, -42.86) * mm});
            skLineSegment(sketch, "E683.MirrorCS", {"start": v(19.84, 26.99) * mm, "end": v(27.78, 26.99) * mm});
            skPoint(sketch, "E684.MirrorP", {"position": v(7.94, -7.94) * mm});
            skArc(sketch, "E685.MirrorCS", {"start": v(35.72, 20.64) * mm, "mid": v(32.54, 23.81) * mm, "end": v(35.72, 26.99) * mm});
            skArc(sketch, "E686.MirrorCS", {"start": v(43.66, -36.51) * mm, "mid": v(46.83, -39.69) * mm, "end": v(43.66, -42.86) * mm});
            skArc(sketch, "E687.MirrorCS", {"start": v(43.66, 4.76) * mm, "mid": v(46.83, 7.94) * mm, "end": v(43.66, 11.11) * mm});
            skArc(sketch, "E688.MirrorCS", {"start": v(11.9, 4.76) * mm, "mid": v(15.08, 7.94) * mm, "end": v(11.9, 11.11) * mm});
            skArc(sketch, "E689.MirrorCS", {"start": v(35.72, -20.64) * mm, "mid": v(32.54, -23.81) * mm, "end": v(35.72, -26.99) * mm});
            skLineSegment(sketch, "E690.MirrorCS", {"start": v(83.34, -11.11) * mm, "end": v(91.28, -11.11) * mm});
            skArc(sketch, "E691.MirrorCS", {"start": v(67.47, -36.51) * mm, "mid": v(64.3, -39.69) * mm, "end": v(67.47, -42.86) * mm});
            skLineSegment(sketch, "E692.MirrorCS", {"start": v(83.34, -4.76) * mm, "end": v(91.28, -4.76) * mm});
            skLineSegment(sketch, "E693.MirrorCS", {"start": v(51.6, -42.86) * mm, "end": v(59.53, -42.86) * mm});
            skArc(sketch, "E694.MirrorCS", {"start": v(43.66, -20.64) * mm, "mid": v(46.83, -23.81) * mm, "end": v(43.66, -26.99) * mm});
            skArc(sketch, "E695.MirrorCS", {"start": v(51.6, 20.64) * mm, "mid": v(48.42, 23.81) * mm, "end": v(51.6, 26.99) * mm});
            skSolve(sketch);
        }
        {
            var Q0;
            Q0 = qSketchRegion(id + "F6", true);
            extrude(context, id + "F7", {"entities" : qUnion([Q0]), "depth" : 3.17 * mm});
        }
        {
            var Q0;
            Q0=makeQuery(id+"F4.opExtrude","SWEPT_FACE",FACE,{"disambiguationData":[OSD([sQuery(id+"F3.wireOp",EDGE,"E231.left")])]});
            var sketch = newSketch(context, id + "F8", { "sketchPlane" : qUnion([Q0])});
            skLineSegment(sketch, "E696", {"start": v(0, 0) * mm, "end": v(34.93, 0) * mm});
            skLineSegment(sketch, "E697", {"start": v(34.93, 0) * mm, "end": v(34.93, 19.05) * mm});
            skLineSegment(sketch, "E698", {"start": v(34.93, 19.05) * mm, "end": v(-34.93, 19.05) * mm});
            skLineSegment(sketch, "E699", {"start": v(-34.93, 19.05) * mm, "end": v(-34.93, 0) * mm});
            skLineSegment(sketch, "E700", {"start": v(-34.93, 0) * mm, "end": v(0, 0) * mm});
            skLineSegment(sketch, "E701", {"start": v(34.93, 19.05) * mm, "end": v(50.8, 19.05) * mm});
            skLineSegment(sketch, "E702", {"start": v(50.8, 19.05) * mm, "end": v(50.8, 28.58) * mm});
            skLineSegment(sketch, "E703", {"start": v(50.8, 28.58) * mm, "end": v(-50.8, 28.57) * mm});
            skLineSegment(sketch, "E704", {"start": v(-50.8, 28.57) * mm, "end": v(-50.8, 19.05) * mm});
            skLineSegment(sketch, "E705", {"start": v(-50.8, 19.05) * mm, "end": v(-34.93, 19.05) * mm});
            skLineSegment(sketch, "E706", {"start": v(-34.93, 0) * mm, "end": v(-50.8, 0) * mm});
            skLineSegment(sketch, "E707", {"start": v(-50.8, 0) * mm, "end": v(-50.8, -3.17) * mm});
            skLineSegment(sketch, "E708", {"start": v(-50.8, -3.17) * mm, "end": v(50.8, -3.17) * mm});
            skLineSegment(sketch, "E709", {"start": v(50.8, -3.17) * mm, "end": v(50.8, 0) * mm});
            skLineSegment(sketch, "E710", {"start": v(50.8, 0) * mm, "end": v(34.93, 0) * mm});
            skSolve(sketch);
        }
        {
            var Q0;
            Q0 = qSketchRegion(id + "F8", true);
            extrude(context, id + "F9", {"entities" : qUnion([Q0]), "oppositeDirection" : true, "depth" : 1 / 203.2 * mm});
        }
        {
            var Q0;
            Q0=makeQuery(id+"F9.opExtrude","SWEPT_BODY",BODY,{"disambiguationData":[OSD([sQuery(id+"F8.wireOp",EDGE,"E697"),sQuery(id+"F8.wireOp",EDGE,"E699"),sQuery(id+"F8.wireOp",EDGE,"E701"),sQuery(id+"F8.wireOp",EDGE,"E702"),sQuery(id+"F8.wireOp",EDGE,"E703"),sQuery(id+"F8.wireOp",EDGE,"E704"),sQuery(id+"F8.wireOp",EDGE,"E705"),sQuery(id+"F8.wireOp",EDGE,"E706"),sQuery(id+"F8.wireOp",EDGE,"E707"),sQuery(id+"F8.wireOp",EDGE,"E708"),sQuery(id+"F8.wireOp",EDGE,"E709"),sQuery(id+"F8.wireOp",EDGE,"E710")])]});
            var Q1;
            Q1=qCreatedBy(makeId("Right.planeOp"),FACE);
            mirror(context, id + "F10", {"entities" : qUnion([Q0]), "mirrorPlane" : qUnion([Q1])});
        }
        {
            var Q0;
            Q0=makeQuery(id+"F9.opExtrude","SWEPT_EDGE",EDGE,{"disambiguationData":[OSD([sQuery(id+"F8.wireOp",EDGE,"E699"),sQuery(id+"F8.wireOp",EDGE,"E700"),sQuery(id+"F8.wireOp",EDGE,"E706")])]});
            var Q1;
            Q1=makeQuery(id+"F9.opExtrude","SWEPT_EDGE",EDGE,{"disambiguationData":[OSD([sQuery(id+"F8.wireOp",EDGE,"E696"),sQuery(id+"F8.wireOp",EDGE,"E697"),sQuery(id+"F8.wireOp",EDGE,"E710")])]});
            var Q2;
            Q2=makeQuery(id+"F9.opExtrude","SWEPT_EDGE",EDGE,{"disambiguationData":[OSD([sQuery(id+"F8.wireOp",EDGE,"E698"),sQuery(id+"F8.wireOp",EDGE,"E699"),sQuery(id+"F8.wireOp",EDGE,"E705")])]});
            var Q3;
            Q3=makeQuery(id+"F9.opExtrude","SWEPT_EDGE",EDGE,{"disambiguationData":[OSD([sQuery(id+"F8.wireOp",EDGE,"E697"),sQuery(id+"F8.wireOp",EDGE,"E698"),sQuery(id+"F8.wireOp",EDGE,"E701")])]});
            var Q4;
            Q4=makeQuery(id+"F10.opPattern","COPY",EDGE,{"derivedFrom":makeQuery(id+"F9.opExtrude","SWEPT_EDGE",EDGE,{"disambiguationData":[OSD([sQuery(id+"F8.wireOp",EDGE,"E697"),sQuery(id+"F8.wireOp",EDGE,"E698"),sQuery(id+"F8.wireOp",EDGE,"E701")])]}),"instanceName":"1"});
            var Q5;
            Q5=makeQuery(id+"F10.opPattern","COPY",EDGE,{"derivedFrom":makeQuery(id+"F9.opExtrude","SWEPT_EDGE",EDGE,{"disambiguationData":[OSD([sQuery(id+"F8.wireOp",EDGE,"E698"),sQuery(id+"F8.wireOp",EDGE,"E699"),sQuery(id+"F8.wireOp",EDGE,"E705")])]}),"instanceName":"1"});
            var Q6;
            Q6=makeQuery(id+"F10.opPattern","COPY",EDGE,{"derivedFrom":makeQuery(id+"F9.opExtrude","SWEPT_EDGE",EDGE,{"disambiguationData":[OSD([sQuery(id+"F8.wireOp",EDGE,"E699"),sQuery(id+"F8.wireOp",EDGE,"E700"),sQuery(id+"F8.wireOp",EDGE,"E706")])]}),"instanceName":"1"});
            var Q7;
            Q7=makeQuery(id+"F10.opPattern","COPY",EDGE,{"derivedFrom":makeQuery(id+"F9.opExtrude","SWEPT_EDGE",EDGE,{"disambiguationData":[OSD([sQuery(id+"F8.wireOp",EDGE,"E696"),sQuery(id+"F8.wireOp",EDGE,"E697"),sQuery(id+"F8.wireOp",EDGE,"E710")])]}),"instanceName":"1"});
            fillet(context, id + "F11", {"entities" : qUnion([Q0, Q1, Q2, Q3, Q4, Q5, Q6, Q7]), "radius" : 5.08 * mm, "tangentPropagation" : true, "allowEdgeOverflow" : false});
        }
        {
            var Q0;
            Q0=makeQuery(id+"F1.opExtrude","SWEPT_FACE",FACE,{"disambiguationData":[OSD([sQuery(id+"F0.wireOp",EDGE,"E0.bottom")])]});
            var sketch = newSketch(context, id + "F12", { "sketchPlane" : qUnion([Q0])});
            skLineSegment(sketch, "E711", {"start": v(0, 0) * mm, "end": v(-63.5, 0) * mm});
            skLineSegment(sketch, "E712", {"start": v(-63.5, 0) * mm, "end": v(-63.5, -25.4) * mm});
            skLineSegment(sketch, "E713", {"start": v(-63.5, -25.4) * mm, "end": v(-57.15, -25.4) * mm});
            skLineSegment(sketch, "E714", {"start": v(-57.15, -25.4) * mm, "end": v(-57.15, 0) * mm});
            skLineSegment(sketch, "E715.MirrorCS", {"start": v(57.15, -25.4) * mm, "end": v(57.15, 0) * mm});
            skLineSegment(sketch, "E716.MirrorCS", {"start": v(63.5, 0) * mm, "end": v(63.5, -25.4) * mm});
            skLineSegment(sketch, "E717.MirrorCS", {"start": v(63.5, -25.4) * mm, "end": v(57.15, -25.4) * mm});
            skLineSegment(sketch, "E718.MirrorCS", {"start": v(0, 0) * mm, "end": v(63.5, 0) * mm});
            skSolve(sketch);
        }
        {
            var Q0;
            Q0 = qSketchRegion(id + "F12", true);
            extrude(context, id + "F13", {"entities" : qUnion([Q0]), "oppositeDirection" : true, "depth" : 1 / 203.2 * mm});
        }
        {
            var Q0;
            Q0=makeQuery(id+"F13.opExtrude","SWEPT_BODY",BODY,{"disambiguationData":[OSD([sQuery(id+"F12.wireOp",EDGE,"E711"),sQuery(id+"F12.wireOp",EDGE,"E712"),sQuery(id+"F12.wireOp",EDGE,"E713"),sQuery(id+"F12.wireOp",EDGE,"E714")])]});
            var Q1;
            Q1=makeQuery(id+"F13.opExtrude","SWEPT_BODY",BODY,{"disambiguationData":[OSD([sQuery(id+"F12.wireOp",EDGE,"E715.MirrorCS"),sQuery(id+"F12.wireOp",EDGE,"E716.MirrorCS"),sQuery(id+"F12.wireOp",EDGE,"E717.MirrorCS"),sQuery(id+"F12.wireOp",EDGE,"E718.MirrorCS")])]});
            var Q2;
            Q2=qCreatedBy(makeId("Front.planeOp"),FACE);
            mirror(context, id + "F14", {"entities" : qUnion([Q0, Q1]), "mirrorPlane" : qUnion([Q2])});
        }
        {
            var Q0;
            Q0=makeQuery(id+"F4.opExtrude","CAP_FACE",FACE,{"disambiguationData":[OSD([sQuery(id+"F3.wireOp",EDGE,"E231.bottom"),sQuery(id+"F3.wireOp",EDGE,"E231.top"),sQuery(id+"F3.wireOp",EDGE,"E231.left"),sQuery(id+"F3.wireOp",EDGE,"E231.right"),sQuery(id+"F3.wireOp",EDGE,"E234.bottom"),sQuery(id+"F3.wireOp",EDGE,"E234.top"),sQuery(id+"F3.wireOp",EDGE,"E234.left"),sQuery(id+"F3.wireOp",EDGE,"E234.right"),sQuery(id+"F3.wireOp",EDGE,"E235.0.1.0"),sQuery(id+"F3.wireOp",EDGE,"E235.0.1.1"),sQuery(id+"F3.wireOp",EDGE,"E235.0.1.2"),sQuery(id+"F3.wireOp",EDGE,"E235.0.1.3"),sQuery(id+"F3.wireOp",EDGE,"E235.0.2.0"),sQuery(id+"F3.wireOp",EDGE,"E235.0.2.1"),sQuery(id+"F3.wireOp",EDGE,"E235.0.2.2"),sQuery(id+"F3.wireOp",EDGE,"E235.0.2.3"),sQuery(id+"F3.wireOp",EDGE,"E235.1.0.0"),sQuery(id+"F3.wireOp",EDGE,"E235.1.0.1"),sQuery(id+"F3.wireOp",EDGE,"E235.1.0.2"),sQuery(id+"F3.wireOp",EDGE,"E235.1.0.3"),sQuery(id+"F3.wireOp",EDGE,"E235.1.1.0"),sQuery(id+"F3.wireOp",EDGE,"E235.1.1.1"),sQuery(id+"F3.wireOp",EDGE,"E235.1.1.2"),sQuery(id+"F3.wireOp",EDGE,"E235.1.1.3"),sQuery(id+"F3.wireOp",EDGE,"E235.1.2.0"),sQuery(id+"F3.wireOp",EDGE,"E235.1.2.1"),sQuery(id+"F3.wireOp",EDGE,"E235.1.2.2"),sQuery(id+"F3.wireOp",EDGE,"E235.1.2.3"),sQuery(id+"F3.wireOp",EDGE,"E235.2.0.0"),sQuery(id+"F3.wireOp",EDGE,"E235.2.0.1"),sQuery(id+"F3.wireOp",EDGE,"E235.2.0.2"),sQuery(id+"F3.wireOp",EDGE,"E235.2.0.3"),sQuery(id+"F3.wireOp",EDGE,"E235.2.1.0"),sQuery(id+"F3.wireOp",EDGE,"E235.2.1.1"),sQuery(id+"F3.wireOp",EDGE,"E235.2.1.2"),sQuery(id+"F3.wireOp",EDGE,"E235.2.1.3"),sQuery(id+"F3.wireOp",EDGE,"E235.2.2.0"),sQuery(id+"F3.wireOp",EDGE,"E235.2.2.1"),sQuery(id+"F3.wireOp",EDGE,"E235.2.2.2"),sQuery(id+"F3.wireOp",EDGE,"E235.2.2.3"),sQuery(id+"F3.wireOp",EDGE,"E235.3.0.0"),sQuery(id+"F3.wireOp",EDGE,"E235.3.0.1"),sQuery(id+"F3.wireOp",EDGE,"E235.3.0.2"),sQuery(id+"F3.wireOp",EDGE,"E235.3.0.3"),sQuery(id+"F3.wireOp",EDGE,"E235.3.1.0"),sQuery(id+"F3.wireOp",EDGE,"E235.3.1.1"),sQuery(id+"F3.wireOp",EDGE,"E235.3.1.2"),sQuery(id+"F3.wireOp",EDGE,"E235.3.1.3"),sQuery(id+"F3.wireOp",EDGE,"E235.3.2.0"),sQuery(id+"F3.wireOp",EDGE,"E235.3.2.1"),sQuery(id+"F3.wireOp",EDGE,"E235.3.2.2"),sQuery(id+"F3.wireOp",EDGE,"E235.3.2.3"),sQuery(id+"F3.wireOp",EDGE,"E235.4.0.0"),sQuery(id+"F3.wireOp",EDGE,"E235.4.0.1"),sQuery(id+"F3.wireOp",EDGE,"E235.4.0.2"),sQuery(id+"F3.wireOp",EDGE,"E235.4.0.3"),sQuery(id+"F3.wireOp",EDGE,"E235.4.1.0"),sQuery(id+"F3.wireOp",EDGE,"E235.4.1.1"),sQuery(id+"F3.wireOp",EDGE,"E235.4.1.2"),sQuery(id+"F3.wireOp",EDGE,"E235.4.1.3"),sQuery(id+"F3.wireOp",EDGE,"E235.4.2.0"),sQuery(id+"F3.wireOp",EDGE,"E235.4.2.1"),sQuery(id+"F3.wireOp",EDGE,"E235.4.2.2"),sQuery(id+"F3.wireOp",EDGE,"E235.4.2.3"),sQuery(id+"F3.wireOp",EDGE,"E235.5.0.0"),sQuery(id+"F3.wireOp",EDGE,"E235.5.0.1"),sQuery(id+"F3.wireOp",EDGE,"E235.5.0.2"),sQuery(id+"F3.wireOp",EDGE,"E235.5.0.3"),sQuery(id+"F3.wireOp",EDGE,"E235.5.1.0"),sQuery(id+"F3.wireOp",EDGE,"E235.5.1.1"),sQuery(id+"F3.wireOp",EDGE,"E235.5.1.2"),sQuery(id+"F3.wireOp",EDGE,"E235.5.1.3"),sQuery(id+"F3.wireOp",EDGE,"E235.5.2.0"),sQuery(id+"F3.wireOp",EDGE,"E235.5.2.1"),sQuery(id+"F3.wireOp",EDGE,"E235.5.2.2"),sQuery(id+"F3.wireOp",EDGE,"E235.5.2.3"),sQuery(id+"F3.wireOp",EDGE,"E237.MirrorCS"),sQuery(id+"F3.wireOp",EDGE,"E238.MirrorCS"),sQuery(id+"F3.wireOp",EDGE,"E239.MirrorCS"),sQuery(id+"F3.wireOp",EDGE,"E240.MirrorCS"),sQuery(id+"F3.wireOp",EDGE,"E241.MirrorCS"),sQuery(id+"F3.wireOp",EDGE,"E242.MirrorCS"),sQuery(id+"F3.wireOp",EDGE,"E243.MirrorCS"),sQuery(id+"F3.wireOp",EDGE,"E244.MirrorCS"),sQuery(id+"F3.wireOp",EDGE,"E245.MirrorCS"),sQuery(id+"F3.wireOp",EDGE,"E246.MirrorCS"),sQuery(id+"F3.wireOp",EDGE,"E247.MirrorCS"),sQuery(id+"F3.wireOp",EDGE,"E248.MirrorCS"),sQuery(id+"F3.wireOp",EDGE,"E249.MirrorCS"),sQuery(id+"F3.wireOp",EDGE,"E250.MirrorCS"),sQuery(id+"F3.wireOp",EDGE,"E251.MirrorCS"),sQuery(id+"F3.wireOp",EDGE,"E252.MirrorCS"),sQuery(id+"F3.wireOp",EDGE,"E253.MirrorCS"),sQuery(id+"F3.wireOp",EDGE,"E254.MirrorCS"),sQuery(id+"F3.wireOp",EDGE,"E255.MirrorCS"),sQuery(id+"F3.wireOp",EDGE,"E256.MirrorCS"),sQuery(id+"F3.wireOp",EDGE,"E257.MirrorCS"),sQuery(id+"F3.wireOp",EDGE,"E258.MirrorCS"),sQuery(id+"F3.wireOp",EDGE,"E259.MirrorCS"),sQuery(id+"F3.wireOp",EDGE,"E260.MirrorCS"),sQuery(id+"F3.wireOp",EDGE,"E261.MirrorCS"),sQuery(id+"F3.wireOp",EDGE,"E262.MirrorCS"),sQuery(id+"F3.wireOp",EDGE,"E263.MirrorCS"),sQuery(id+"F3.wireOp",EDGE,"E264.MirrorCS"),sQuery(id+"F3.wireOp",EDGE,"E265.MirrorCS"),sQuery(id+"F3.wireOp",EDGE,"E266.MirrorCS"),sQuery(id+"F3.wireOp",EDGE,"E267.MirrorCS"),sQuery(id+"F3.wireOp",EDGE,"E268.MirrorCS"),sQuery(id+"F3.wireOp",EDGE,"E269.MirrorCS"),sQuery(id+"F3.wireOp",EDGE,"E270.MirrorCS"),sQuery(id+"F3.wireOp",EDGE,"E271.MirrorCS"),sQuery(id+"F3.wireOp",EDGE,"E272.MirrorCS"),sQuery(id+"F3.wireOp",EDGE,"E273.MirrorCS"),sQuery(id+"F3.wireOp",EDGE,"E274.MirrorCS"),sQuery(id+"F3.wireOp",EDGE,"E275.MirrorCS"),sQuery(id+"F3.wireOp",EDGE,"E276.MirrorCS"),sQuery(id+"F3.wireOp",EDGE,"E277.MirrorCS"),sQuery(id+"F3.wireOp",EDGE,"E278.MirrorCS"),sQuery(id+"F3.wireOp",EDGE,"E279.MirrorCS"),sQuery(id+"F3.wireOp",EDGE,"E280.MirrorCS"),sQuery(id+"F3.wireOp",EDGE,"E281.MirrorCS"),sQuery(id+"F3.wireOp",EDGE,"E282.MirrorCS"),sQuery(id+"F3.wireOp",EDGE,"E283.MirrorCS"),sQuery(id+"F3.wireOp",EDGE,"E285.MirrorCS"),sQuery(id+"F3.wireOp",EDGE,"E286.MirrorCS"),sQuery(id+"F3.wireOp",EDGE,"E287.MirrorCS"),sQuery(id+"F3.wireOp",EDGE,"E288.MirrorCS"),sQuery(id+"F3.wireOp",EDGE,"E289.MirrorCS"),sQuery(id+"F3.wireOp",EDGE,"E290.MirrorCS"),sQuery(id+"F3.wireOp",EDGE,"E291.MirrorCS"),sQuery(id+"F3.wireOp",EDGE,"E292.MirrorCS"),sQuery(id+"F3.wireOp",EDGE,"E293.MirrorCS"),sQuery(id+"F3.wireOp",EDGE,"E294.MirrorCS"),sQuery(id+"F3.wireOp",EDGE,"E295.MirrorCS"),sQuery(id+"F3.wireOp",EDGE,"E296.MirrorCS"),sQuery(id+"F3.wireOp",EDGE,"E297.MirrorCS"),sQuery(id+"F3.wireOp",EDGE,"E298.MirrorCS"),sQuery(id+"F3.wireOp",EDGE,"E299.MirrorCS"),sQuery(id+"F3.wireOp",EDGE,"E300.MirrorCS"),sQuery(id+"F3.wireOp",EDGE,"E302.MirrorCS"),sQuery(id+"F3.wireOp",EDGE,"E303.MirrorCS"),sQuery(id+"F3.wireOp",EDGE,"E304.MirrorCS"),sQuery(id+"F3.wireOp",EDGE,"E305.MirrorCS"),sQuery(id+"F3.wireOp",EDGE,"E306.MirrorCS"),sQuery(id+"F3.wireOp",EDGE,"E307.MirrorCS"),sQuery(id+"F3.wireOp",EDGE,"E308.MirrorCS"),sQuery(id+"F3.wireOp",EDGE,"E309.MirrorCS"),sQuery(id+"F3.wireOp",EDGE,"E310.MirrorCS"),sQuery(id+"F3.wireOp",EDGE,"E313.MirrorCS"),sQuery(id+"F3.wireOp",EDGE,"E315.MirrorCS"),sQuery(id+"F3.wireOp",EDGE,"E316.MirrorCS"),sQuery(id+"F3.wireOp",EDGE,"E318.MirrorCS"),sQuery(id+"F3.wireOp",EDGE,"E319.MirrorCS"),sQuery(id+"F3.wireOp",EDGE,"E320.MirrorCS"),sQuery(id+"F3.wireOp",EDGE,"E321.MirrorCS"),sQuery(id+"F3.wireOp",EDGE,"E322.MirrorCS"),sQuery(id+"F3.wireOp",EDGE,"E323.MirrorCS"),sQuery(id+"F3.wireOp",EDGE,"E324.MirrorCS"),sQuery(id+"F3.wireOp",EDGE,"E325.MirrorCS"),sQuery(id+"F3.wireOp",EDGE,"E326.MirrorCS"),sQuery(id+"F3.wireOp",EDGE,"E327.MirrorCS"),sQuery(id+"F3.wireOp",EDGE,"E328.MirrorCS"),sQuery(id+"F3.wireOp",EDGE,"E329.MirrorCS"),sQuery(id+"F3.wireOp",EDGE,"E330.MirrorCS"),sQuery(id+"F3.wireOp",EDGE,"E331.MirrorCS"),sQuery(id+"F3.wireOp",EDGE,"E332.MirrorCS"),sQuery(id+"F3.wireOp",EDGE,"E333.MirrorCS"),sQuery(id+"F3.wireOp",EDGE,"E334.MirrorCS"),sQuery(id+"F3.wireOp",EDGE,"E335.MirrorCS"),sQuery(id+"F3.wireOp",EDGE,"E336.MirrorCS"),sQuery(id+"F3.wireOp",EDGE,"E337.MirrorCS"),sQuery(id+"F3.wireOp",EDGE,"E338.MirrorCS"),sQuery(id+"F3.wireOp",EDGE,"E339.MirrorCS"),sQuery(id+"F3.wireOp",EDGE,"E340.MirrorCS"),sQuery(id+"F3.wireOp",EDGE,"E341.MirrorCS"),sQuery(id+"F3.wireOp",EDGE,"E342.MirrorCS"),sQuery(id+"F3.wireOp",EDGE,"E343.MirrorCS"),sQuery(id+"F3.wireOp",EDGE,"E344.MirrorCS"),sQuery(id+"F3.wireOp",EDGE,"E345.MirrorCS"),sQuery(id+"F3.wireOp",EDGE,"E346.MirrorCS"),sQuery(id+"F3.wireOp",EDGE,"E347.MirrorCS"),sQuery(id+"F3.wireOp",EDGE,"E348.MirrorCS"),sQuery(id+"F3.wireOp",EDGE,"E349.MirrorCS"),sQuery(id+"F3.wireOp",EDGE,"E350.MirrorCS"),sQuery(id+"F3.wireOp",EDGE,"E351.MirrorCS"),sQuery(id+"F3.wireOp",EDGE,"E352.MirrorCS"),sQuery(id+"F3.wireOp",EDGE,"E353.MirrorCS"),sQuery(id+"F3.wireOp",EDGE,"E354.MirrorCS"),sQuery(id+"F3.wireOp",EDGE,"E355.MirrorCS"),sQuery(id+"F3.wireOp",EDGE,"E356.MirrorCS"),sQuery(id+"F3.wireOp",EDGE,"E357.MirrorCS"),sQuery(id+"F3.wireOp",EDGE,"E358.MirrorCS"),sQuery(id+"F3.wireOp",EDGE,"E359.MirrorCS"),sQuery(id+"F3.wireOp",EDGE,"E360.MirrorCS"),sQuery(id+"F3.wireOp",EDGE,"E361.MirrorCS"),sQuery(id+"F3.wireOp",EDGE,"E362.MirrorCS"),sQuery(id+"F3.wireOp",EDGE,"E363.MirrorCS"),sQuery(id+"F3.wireOp",EDGE,"E365.MirrorCS"),sQuery(id+"F3.wireOp",EDGE,"E366.MirrorCS"),sQuery(id+"F3.wireOp",EDGE,"E367.MirrorCS"),sQuery(id+"F3.wireOp",EDGE,"E368.MirrorCS"),sQuery(id+"F3.wireOp",EDGE,"E369.MirrorCS"),sQuery(id+"F3.wireOp",EDGE,"E370.MirrorCS"),sQuery(id+"F3.wireOp",EDGE,"E371.MirrorCS"),sQuery(id+"F3.wireOp",EDGE,"E372.MirrorCS"),sQuery(id+"F3.wireOp",EDGE,"E373.MirrorCS"),sQuery(id+"F3.wireOp",EDGE,"E374.MirrorCS"),sQuery(id+"F3.wireOp",EDGE,"E375.MirrorCS"),sQuery(id+"F3.wireOp",EDGE,"E376.MirrorCS"),sQuery(id+"F3.wireOp",EDGE,"E377.MirrorCS"),sQuery(id+"F3.wireOp",EDGE,"E378.MirrorCS"),sQuery(id+"F3.wireOp",EDGE,"E379.MirrorCS"),sQuery(id+"F3.wireOp",EDGE,"E380.MirrorCS"),sQuery(id+"F3.wireOp",EDGE,"E381.MirrorCS"),sQuery(id+"F3.wireOp",EDGE,"E383.MirrorCS"),sQuery(id+"F3.wireOp",EDGE,"E384.MirrorCS"),sQuery(id+"F3.wireOp",EDGE,"E385.MirrorCS"),sQuery(id+"F3.wireOp",EDGE,"E386.MirrorCS"),sQuery(id+"F3.wireOp",EDGE,"E387.MirrorCS"),sQuery(id+"F3.wireOp",EDGE,"E388.MirrorCS"),sQuery(id+"F3.wireOp",EDGE,"E389.MirrorCS"),sQuery(id+"F3.wireOp",EDGE,"E390.MirrorCS"),sQuery(id+"F3.wireOp",EDGE,"E391.MirrorCS"),sQuery(id+"F3.wireOp",EDGE,"E392.MirrorCS"),sQuery(id+"F3.wireOp",EDGE,"E393.MirrorCS"),sQuery(id+"F3.wireOp",EDGE,"E394.MirrorCS"),sQuery(id+"F3.wireOp",EDGE,"E395.MirrorCS"),sQuery(id+"F3.wireOp",EDGE,"E396.MirrorCS"),sQuery(id+"F3.wireOp",EDGE,"E397.MirrorCS"),sQuery(id+"F3.wireOp",EDGE,"E398.MirrorCS"),sQuery(id+"F3.wireOp",EDGE,"E399.MirrorCS"),sQuery(id+"F3.wireOp",EDGE,"E400.MirrorCS"),sQuery(id+"F3.wireOp",EDGE,"E401.MirrorCS"),sQuery(id+"F3.wireOp",EDGE,"E402.MirrorCS"),sQuery(id+"F3.wireOp",EDGE,"E403.MirrorCS"),sQuery(id+"F3.wireOp",EDGE,"E404.MirrorCS"),sQuery(id+"F3.wireOp",EDGE,"E405.MirrorCS"),sQuery(id+"F3.wireOp",EDGE,"E406.MirrorCS"),sQuery(id+"F3.wireOp",EDGE,"E407.MirrorCS"),sQuery(id+"F3.wireOp",EDGE,"E408.MirrorCS"),sQuery(id+"F3.wireOp",EDGE,"E409.MirrorCS"),sQuery(id+"F3.wireOp",EDGE,"E410.MirrorCS"),sQuery(id+"F3.wireOp",EDGE,"E411.MirrorCS"),sQuery(id+"F3.wireOp",EDGE,"E412.MirrorCS"),sQuery(id+"F3.wireOp",EDGE,"E413.MirrorCS"),sQuery(id+"F3.wireOp",EDGE,"E414.MirrorCS"),sQuery(id+"F3.wireOp",EDGE,"E415.MirrorCS"),sQuery(id+"F3.wireOp",EDGE,"E416.MirrorCS"),sQuery(id+"F3.wireOp",EDGE,"E417.MirrorCS"),sQuery(id+"F3.wireOp",EDGE,"E418.MirrorCS"),sQuery(id+"F3.wireOp",EDGE,"E419.MirrorCS"),sQuery(id+"F3.wireOp",EDGE,"E420.MirrorCS"),sQuery(id+"F3.wireOp",EDGE,"E421.MirrorCS"),sQuery(id+"F3.wireOp",EDGE,"E422.MirrorCS"),sQuery(id+"F3.wireOp",EDGE,"E424.MirrorCS"),sQuery(id+"F3.wireOp",EDGE,"E425.MirrorCS"),sQuery(id+"F3.wireOp",EDGE,"E426.MirrorCS"),sQuery(id+"F3.wireOp",EDGE,"E427.MirrorCS"),sQuery(id+"F3.wireOp",EDGE,"E428.MirrorCS"),sQuery(id+"F3.wireOp",EDGE,"E429.MirrorCS"),sQuery(id+"F3.wireOp",EDGE,"E430.MirrorCS"),sQuery(id+"F3.wireOp",EDGE,"E431.MirrorCS"),sQuery(id+"F3.wireOp",EDGE,"E432.MirrorCS"),sQuery(id+"F3.wireOp",EDGE,"E433.MirrorCS"),sQuery(id+"F3.wireOp",EDGE,"E434.MirrorCS"),sQuery(id+"F3.wireOp",EDGE,"E435.MirrorCS"),sQuery(id+"F3.wireOp",EDGE,"E436.MirrorCS"),sQuery(id+"F3.wireOp",EDGE,"E437.MirrorCS"),sQuery(id+"F3.wireOp",EDGE,"E438.MirrorCS"),sQuery(id+"F3.wireOp",EDGE,"E439.MirrorCS"),sQuery(id+"F3.wireOp",EDGE,"E440.MirrorCS"),sQuery(id+"F3.wireOp",EDGE,"E441.MirrorCS"),sQuery(id+"F3.wireOp",EDGE,"E442.MirrorCS"),sQuery(id+"F3.wireOp",EDGE,"E443.MirrorCS"),sQuery(id+"F3.wireOp",EDGE,"E444.MirrorCS"),sQuery(id+"F3.wireOp",EDGE,"E445.MirrorCS"),sQuery(id+"F3.wireOp",EDGE,"E446.MirrorCS"),sQuery(id+"F3.wireOp",EDGE,"E447.MirrorCS"),sQuery(id+"F3.wireOp",EDGE,"E448.MirrorCS"),sQuery(id+"F3.wireOp",EDGE,"E449.MirrorCS"),sQuery(id+"F3.wireOp",EDGE,"E450.MirrorCS"),sQuery(id+"F3.wireOp",EDGE,"E451.MirrorCS"),sQuery(id+"F3.wireOp",EDGE,"E452.MirrorCS"),sQuery(id+"F3.wireOp",EDGE,"E453.MirrorCS"),sQuery(id+"F3.wireOp",EDGE,"E454.MirrorCS"),sQuery(id+"F3.wireOp",EDGE,"E455.MirrorCS"),sQuery(id+"F3.wireOp",EDGE,"E456.MirrorCS"),sQuery(id+"F3.wireOp",EDGE,"E457.MirrorCS"),sQuery(id+"F3.wireOp",EDGE,"E458.MirrorCS"),sQuery(id+"F3.wireOp",EDGE,"E459.MirrorCS"),sQuery(id+"F3.wireOp",EDGE,"E460.MirrorCS"),sQuery(id+"F3.wireOp",EDGE,"E461.MirrorCS")])],"isStart":false});
            var sketch = newSketch(context, id + "F15", { "sketchPlane" : qUnion([Q0])});
            skLineSegment(sketch, "E719.bottom", {"start": v(2.54, -1.59) * mm, "end": v(-2.54, -1.59) * mm});
            skLineSegment(sketch, "E719.top", {"start": v(2.54, 1.59) * mm, "end": v(-2.54, 1.59) * mm});
            skLineSegment(sketch, "E719.left", {"start": v(2.54, -1.59) * mm, "end": v(2.54, 1.59) * mm});
            skLineSegment(sketch, "E719.right", {"start": v(-2.54, -1.59) * mm, "end": v(-2.54, 1.59) * mm});
            skPoint(sketch, "E719.middle", {"position": v(0, 0) * mm});
            skLineSegment(sketch, "E720.bottom", {"start": v(1.59, -2.54) * mm, "end": v(-1.59, -2.54) * mm});
            skLineSegment(sketch, "E720.top", {"start": v(1.59, 2.54) * mm, "end": v(-1.59, 2.54) * mm});
            skLineSegment(sketch, "E720.left", {"start": v(1.59, -2.54) * mm, "end": v(1.59, 2.54) * mm});
            skLineSegment(sketch, "E720.right", {"start": v(-1.59, -2.54) * mm, "end": v(-1.59, 2.54) * mm});
            skSolve(sketch);
        }
        {
            var Q0;
            Q0 = qSketchRegion(id + "F15", true);
            extrude(context, id + "F16", {"entities" : qUnion([Q0]), "oppositeDirection" : true, "depth" : 50.8 * mm});
        }
    });
